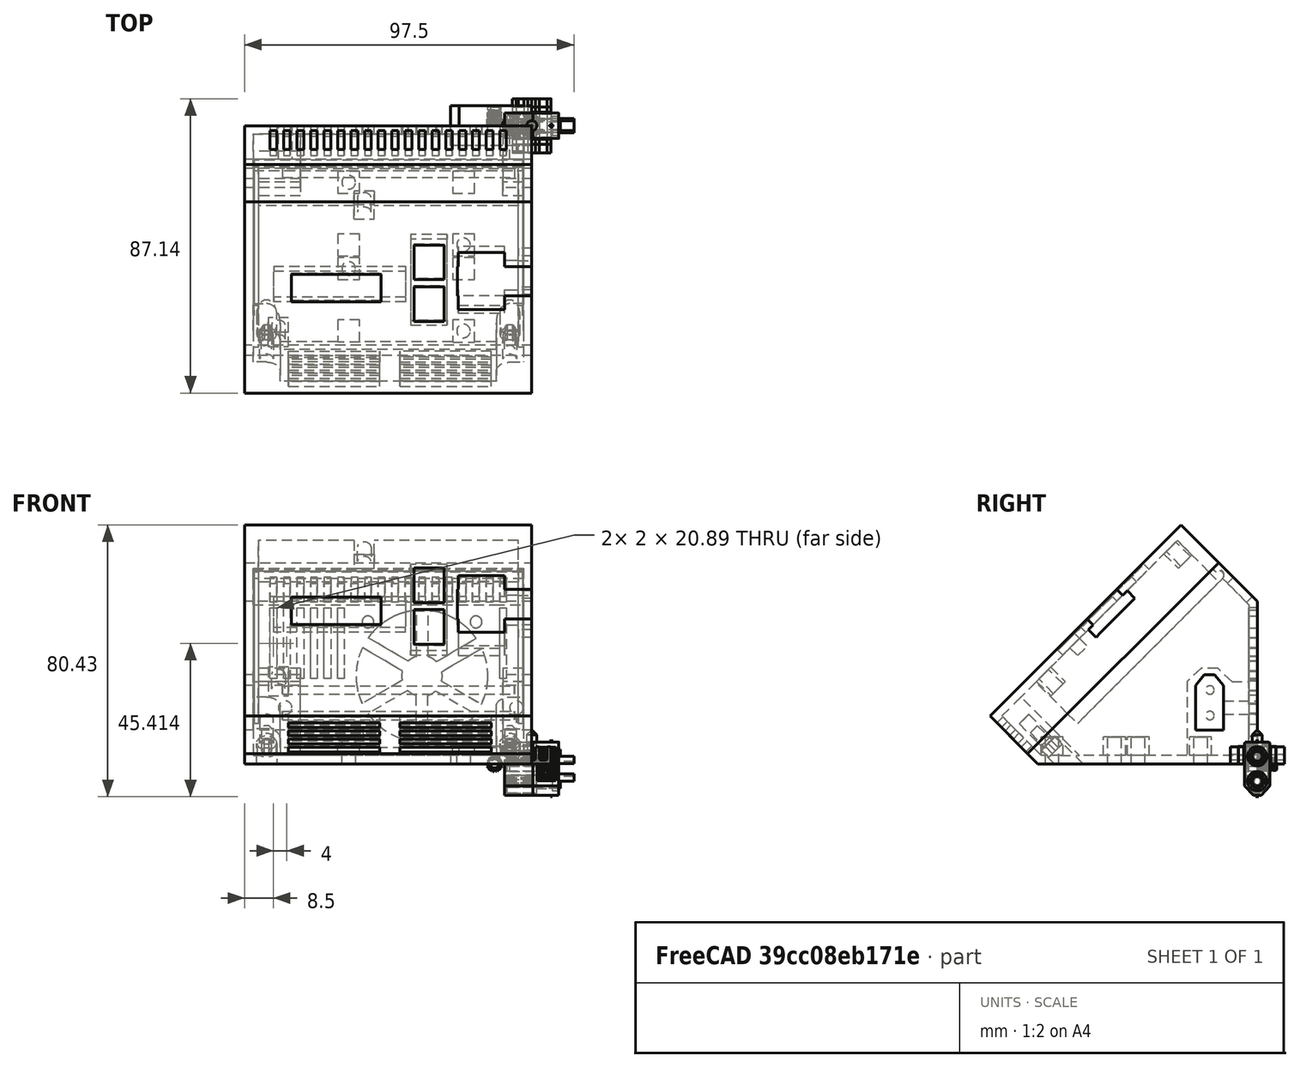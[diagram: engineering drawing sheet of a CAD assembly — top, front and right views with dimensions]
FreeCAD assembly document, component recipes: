
FREECAD ASSEMBLY — COMPONENT RECIPES ("moduleUSB3A_023_SurBase35mm_013")

This assembly document has 20 components, labeled P0..P19 below (a component is one placed body or linked part). 13 of them carry a construction recipe — the FreeCAD feature program that regenerates the part from scratch, quoted from this document or its linked companion documents; the rest are supplied as boundary geometry only. No exploded tour is included for this assembly.
COMPONENT P0 — recipe-attached ("base", modeled in this document).
Construction recipe (the document's own serialized feature program — sketch geometry with constraints, then the solid features built on it; lengths are millimeters unless a unit is written):

FEATURE [PartDesign::FeatureBase] Clone
  BaseFeature = -> Slice_child0
FEATURE [PartDesign::Thickness] Thickness
  Base = -> Clone [Face7]
  BaseFeature = -> Clone
  Intersection = false
  Join = 0
  Mode = 0
  Reversed = true
  SupportTransform = false
  Value = 2.5
  expr: Value = <<sp>>.epaisseurParois
FEATURE [PartDesign::Plane] DatumPlane001  label="planXt"
  AttachmentOffset = pos=(0,0,-2.5) rot=(0,0,1;0rad)
  Length = 110.737
  MapMode = 5
  Placement = pos=(-2.5,6e-16,-6e-16) rot=(0.57735,0.57735,0.57735;2.0944rad)
  ResizeMode = 0
  Support = -> [YZ_Plane002]
  Width = 102.305
  expr: .AttachmentOffset.Base.z = -<<sp>>.epaisseurParois
FEATURE [Sketcher::SketchObject] Sketch002  label="sk_renfortXt"
  FullyConstrained = true
  MapMode = 5
  Placement = pos=(-2.5,6e-16,-6e-16) rot=(0.57735,0.57735,0.57735;2.0944rad)
  Support = -> [DatumPlane001]
  expr: .Constraints.dist = <<sp>>.xt60distanceAngleBord
  expr: .Constraints.epRf = <<sp>>.xt60epRenfort
  expr: Constraints[13] = <<sp>>.xt60largeurFetiere
  expr: Constraints[14] = <<sp>>.xt60hauteur
  expr: Constraints[15] = <<sp>>.xt60hauteurToit
  expr: Constraints[16] = <<sp>>.xt60base
  expr: Constraints[18] = .Constraints.dist
  expr: Constraints[31] = <<sp>>.epaisseurParois
  expr: Constraints[32] = .Constraints.epRf
  expr: Constraints[34] = .Constraints.epRf
  expr: Constraints[45] = <<sp>>.epaisseurParois
  sketch-geometry (17):
    g0: LineSegment StartX=-18.3 StartY=10 StartZ=0 EndX=-18.3 EndY=23.25 EndZ=0
    g1: LineSegment StartX=-18.3 StartY=23.25 StartZ=0 EndX=-15.65 EndY=25.75 EndZ=0
    g2: LineSegment StartX=-15.65 StartY=25.75 StartZ=0 EndX=-12.65 EndY=25.75 EndZ=0
    g3: LineSegment StartX=-12.65 StartY=25.75 StartZ=0 EndX=-10 EndY=23.25 EndZ=0
    g4: LineSegment StartX=-10 StartY=23.25 StartZ=0 EndX=-10 EndY=10 EndZ=0
    g5: LineSegment StartX=-10 StartY=10 StartZ=0 EndX=-18.3 EndY=10 EndZ=0
    g6: LineSegment StartX=-14.15 StartY=10 StartZ=0 EndX=-14.15 EndY=25.75 EndZ=0
    g7: LineSegment StartX=-16.6431 StartY=28.25 StartZ=0 EndX=-20.8 EndY=24.3284 EndZ=0
    g8: LineSegment StartX=-20.8 StartY=24.3284 StartZ=0 EndX=-20.8 EndY=2.5 EndZ=0
    g9: LineSegment StartX=-20.8 StartY=2.5 StartZ=0 EndX=-7.5 EndY=2.5 EndZ=0
    g10: LineSegment StartX=-7.5 StartY=2.5 StartZ=0 EndX=-7.5 EndY=24.3284 EndZ=0
    g11: LineSegment StartX=-7.5 StartY=24.3284 StartZ=0 EndX=-11.6569 EndY=28.25 EndZ=0
    g12: LineSegment StartX=-11.6569 StartY=28.25 StartZ=0 EndX=-16.6431 EndY=28.25 EndZ=0
    g13: LineSegment StartX=-7.5 StartY=24.3284 StartZ=0 EndX=-2.5 EndY=24.3284 EndZ=0
    g14: LineSegment StartX=-2.5 StartY=24.3284 StartZ=0 EndX=-2.5 EndY=2.5 EndZ=0
    g15: LineSegment StartX=-2.5 StartY=2.5 StartZ=0 EndX=-7.5 EndY=2.5 EndZ=0
    g16: LineSegment StartX=-7.5 StartY=2.5 StartZ=0 EndX=-7.5 EndY=24.3284 EndZ=0
  constraints (46):
    c: Vertical(g0)
    c: Coincident(g0,g1)
    c: Coincident(g1,g2)
    c: Horizontal(g2)
    c: Coincident(g2,g3)
    c: Coincident(g3,g4)
    c: Vertical(g4)
    c: Coincident(g4,g5)
    c: Coincident(g5,g0)
    c: Horizontal(g5)
    c: Symmetric(g1,g2,g6)
    c: Equal(g0,g4)
    c: Symmetric(g0,g4,g6)
    c: DistanceX(g2,g2) = 3
    c: DistanceY(g4,g4) = 13.25
    c: DistanceY(g3,g2) = 2.5
    c: DistanceX(g5,g5) = 8.3
    c: DistanceX(g4,g-1) = 10  'dist'
    c: DistanceY(g-1,g4) = 10
    c: Coincident(g7,g8)
    c: Vertical(g8)
    c: Coincident(g8,g9)
    c: Horizontal(g9)
    c: Coincident(g9,g10)
    c: Coincident(g10,g11)
    c: Coincident(g11,g12)
    c: Coincident(g12,g7)
    c: Symmetric(g7,g10,g6)
    c: Symmetric(g7,g11,g6)
    c: Symmetric(g8,g9,g6)
    c: DistanceX(g8,g0) = 2.5  'epRf'
    c: DistanceY(g-1,g9) = 2.5
    c: Distance(g7,g1) = 2.5
    c: Parallel(g1,g7)
    c: DistanceY(g2,g11) = 2.5
    c: Coincident(g13,g14)
    c: Coincident(g14,g15)
    c: Coincident(g15,g16)
    c: Coincident(g16,g13)
    c: Horizontal(g13)
    c: Horizontal(g15)
    c: Vertical(g14)
    c: Vertical(g16)
    c: Coincident(g13,g11)
    c: Horizontal(g14,g9)
    c: DistanceX(g14,g-1) = 2.5
FEATURE [PartDesign::Pad] Pad001  label="renfortXt"
  AllowMultiFace = false
  BaseFeature = -> Thickness
  Direction = (1,-1e-16,1e-16)
  Length = 80
  Length2 = 100
  Profile = -> Sketch002
  Reversed = true
  Type = 0
  expr: Length = <<sp>>.largeurModuleBase - 2 * <<sp>>.epaisseurParois
FEATURE [Sketcher::SketchObject] Sketch003  label="sk_trouXt"
  FullyConstrained = true
  MapMode = 5
  Placement = pos=(0,0,0) rot=(0.57735,0.57735,0.57735;2.0944rad)
  Support = -> [YZ_Plane002]
  expr: .Constraints.dist = <<sp>>.xt60distanceAngleBord
  expr: Constraints[13] = <<sp>>.xt60base
  expr: Constraints[14] = <<sp>>.xt60hauteur
  expr: Constraints[15] = <<sp>>.xt60hauteurToit + <<sp>>.xtJeu
  expr: Constraints[16] = <<sp>>.xt60largeurFetiere
  expr: Constraints[18] = .Constraints.dist
  sketch-geometry (7):
    g0: LineSegment StartX=-18.3 StartY=10 StartZ=0 EndX=-18.3 EndY=23.25 EndZ=0
    g1: LineSegment StartX=-18.3 StartY=23.25 StartZ=0 EndX=-15.65 EndY=26.35 EndZ=0
    g2: LineSegment StartX=-15.65 StartY=26.35 StartZ=0 EndX=-12.65 EndY=26.35 EndZ=0
    g3: LineSegment StartX=-12.65 StartY=26.35 StartZ=0 EndX=-10 EndY=23.25 EndZ=0
    g4: LineSegment StartX=-10 StartY=23.25 StartZ=0 EndX=-10 EndY=10 EndZ=0
    g5: LineSegment StartX=-10 StartY=10 StartZ=0 EndX=-18.3 EndY=10 EndZ=0
    g6: LineSegment StartX=-14.15 StartY=10 StartZ=0 EndX=-14.15 EndY=26.35 EndZ=0
  constraints (19):
    c: Vertical(g0)
    c: Coincident(g0,g1)
    c: Coincident(g1,g2)
    c: Horizontal(g2)
    c: Coincident(g2,g3)
    c: Coincident(g3,g4)
    c: Coincident(g4,g5)
    c: Coincident(g5,g0)
    c: Horizontal(g5)
    c: Symmetric(g1,g2,g6)
    c: Symmetric(g0,g3,g6)
    c: Vertical(g6)
    c: Symmetric(g0,g4,g6)
    c: DistanceX(g5,g5) = 8.3
    c: DistanceY(g4,g4) = 13.25
    c: DistanceY(g3,g2) = 3.1
    c: DistanceX(g2,g2) = 3
    c: DistanceX(g4,g-1) = 10  'dist'
    c: DistanceY(g-1,g4) = 10
FEATURE [PartDesign::Pocket] Pocket
  AllowMultiFace = false
  BaseFeature = -> Pad001
  Direction = (-1,2e-16,-3e-16)
  Length = 85
  Length2 = 100
  Profile = -> Sketch003
  Type = 0
  expr: Length = <<sp>>.largeurModuleBase
FEATURE [PartDesign::Plane] DatumPlane002  label="planDecoupeRenfortXt"
  AttachmentOffset = pos=(0,0,2.5) rot=(0,0,1;0rad)
  Length = 129.29
  MapMode = 5
  Placement = pos=(0,-2.5,-6e-16) rot=(1,0,0;1.5708rad)
  ResizeMode = 0
  Support = -> [XZ_Plane002]
  Width = 103.858
  expr: .AttachmentOffset.Base.z = <<sp>>.epaisseurParois
FEATURE [Sketcher::SketchObject] Sketch004  label="sk_decoupRenfXt"
  FullyConstrained = true
  MapMode = 5
  Placement = pos=(0,-2.5,-6e-16) rot=(1,0,0;1.5708rad)
  Support = -> [DatumPlane002]
  expr: Constraints[10] = <<sp>>.xt60LongueurRenfortPetit + <<sp>>.epaisseurParois
  expr: Constraints[11] = <<sp>>.largeurModuleBase - (<<sp>>.xt60longueurRenfortGrand + <<sp>>.epaisseurParois)
  expr: Constraints[8] = <<sp>>.epaisseurParois
  expr: Constraints[9] = <<sp>>.xt60distanceAngleBord + <<sp>>.xt60hauteur + <<sp>>.xt60hauteurToit + <<sp>>.xt60epRenfort
  sketch-geometry (4):
    g0: LineSegment StartX=-68.5 StartY=28.25 StartZ=0 EndX=-8.5 EndY=28.25 EndZ=0
    g1: LineSegment StartX=-8.5 StartY=28.25 StartZ=0 EndX=-8.5 EndY=2.5 EndZ=0
    g2: LineSegment StartX=-8.5 StartY=2.5 StartZ=0 EndX=-68.5 EndY=2.5 EndZ=0
    g3: LineSegment StartX=-68.5 StartY=2.5 StartZ=0 EndX=-68.5 EndY=28.25 EndZ=0
  constraints (12):
    c: Coincident(g0,g1)
    c: Coincident(g1,g2)
    c: Coincident(g2,g3)
    c: Coincident(g3,g0)
    c: Horizontal(g0)
    c: Horizontal(g2)
    c: Vertical(g1)
    c: Vertical(g3)
    c: DistanceY(g-1,g1) = 2.5
    c: DistanceY(g-1,g0) = 28.25
    c: DistanceX(g1,g-1) = 8.5
    c: DistanceX(g2,g-1) = 68.5
FEATURE [PartDesign::Pocket] Pocket001  label="decoupeRenfXt"
  AllowMultiFace = false
  BaseFeature = -> Pocket
  Direction = (0,1,2e-16)
  Length = 23.3
  Length2 = 100
  Profile = -> Sketch004
  Reversed = true
  Type = 0
  expr: Length = <<sp>>.xt60distanceAngleBord + <<sp>>.xt60base + 2 * <<sp>>.xt60epRenfort
FEATURE [Sketcher::SketchObject] Sketch005  label="xt60PercagePostMale"
  FullyConstrained = true
  MapMode = 5
  Placement = pos=(0,0,0) rot=(1,0,0;1.5708rad)
  Support = -> [XZ_Plane002]
  expr: Constraints[0] = <<sp>>.insertDiamPercage
  expr: Constraints[1] = <<sp>>.insertDistanceTrouBordMale
  expr: Constraints[2] = <<sp>>.insertHauteur
  sketch-geometry (1):
    g0: Circle CenterX=-4.5 CenterY=16.625 CenterZ=0 NormalX=0 NormalY=0 NormalZ=1 AngleXU=0 Radius=2
  constraints (3):
    c: Diameter(g0) = 4
    c: DistanceX(g0,g-1) = 4.5
    c: DistanceY(g-1,g0) = 16.625
FEATURE [PartDesign::Pocket] Pocket002  label="insertXtMale"
  AllowMultiFace = false
  BaseFeature = -> Pocket001
  Direction = (0,1,2e-16)
  Length = 10
  Length2 = 100
  Profile = -> Sketch005
  Reversed = true
  Type = 0
  expr: Length = <<sp>>.insertProfondeurPercage
FEATURE [Sketcher::SketchObject] Sketch006  label="xt60PercagePostFem"
  FullyConstrained = true
  MapMode = 5
  Placement = pos=(0,0,0) rot=(1,0,0;1.5708rad)
  Support = -> [XZ_Plane002]
  expr: Constraints[0] = <<sp>>.insertDiamPercage
  expr: Constraints[1] = <<sp>>.insertDistanceTrouBordFem
  expr: Constraints[2] = <<sp>>.insertHauteur
  sketch-geometry (1):
    g0: Circle CenterX=-73 CenterY=16.625 CenterZ=0 NormalX=0 NormalY=0 NormalZ=1 AngleXU=0 Radius=2
  constraints (3):
    c: Diameter(g0) = 4
    c: DistanceX(g0,g-1) = 73
    c: DistanceY(g-1,g0) = 16.625
FEATURE [PartDesign::Pocket] Pocket003  label="insertXt60Fem"
  AllowMultiFace = false
  BaseFeature = -> Pocket002
  Direction = (0,1,2e-16)
  Length = 10
  Length2 = 100
  Profile = -> Sketch006
  Reversed = true
  Type = 0
  expr: Length = <<sp>>.insertProfondeurPercage
FEATURE [PartDesign::Plane] DatumPlane003
  AttachmentOffset = pos=(0,0,2.5) rot=(0,0,1;0rad)
  Length = 130.229
  MapMode = 2
  Placement = pos=(0,0,2.5) rot=(0,0,1;0rad)
  ResizeMode = 0
  Support = -> [XY_Plane002]
  Width = 113.229
  expr: .AttachmentOffset.Base.z = <<sp>>.epaisseurParois
FEATURE [PartDesign::Plane] DatumPlane004  label="planTrancheur"
  AttachmentOffset = pos=(0,0,71) rot=(-1,0,0;0.785398rad)
  Length = 133.505
  MapMode = 5
  Placement = pos=(0,-71,-1.58e-14) rot=(1,0,0;0.785398rad)
  ResizeMode = 0
  Support = -> [XZ_Plane002]
  Width = 149.064
  expr: .AttachmentOffset.Base.z = <<sp>>.planTrancheur
FEATURE [Sketcher::SketchObject] Sketch008
  FullyConstrained = true
  MapMode = 5
  Placement = pos=(0,-71,-2.13e-14) rot=(1,0,0;0.785398rad)
  Support = -> [DatumPlane004]
  expr: .Constraints.dist = <<sp>>.epaisseurParois
  expr: Constraints[13] = <<sp>>.epaisseurParois
  expr: Constraints[16] = <<sp>>.insertDiamPercage / 2 + <<sp>>.insertFAVMargeDist
  expr: Constraints[1] = <<sp>>.insertFavDistAuZeroDuPLan
  expr: Constraints[21] = <<sp>>.insertFAVDistBord
  expr: Constraints[22] = <<sp>>.largeurModuleBase - <<sp>>.epaisseurParois
  sketch-geometry (7):
    g0: LineSegment StartX=-2.5 StartY=4.24264 StartZ=0 EndX=-82.5 EndY=4.24264 EndZ=0
    g1: LineSegment StartX=-6.5 StartY=14.7426 StartZ=0 EndX=-2.5 EndY=14.7426 EndZ=0
    g2: LineSegment StartX=-2.5 StartY=14.7426 StartZ=0 EndX=-2.5 EndY=6.74264 EndZ=0
    g3: LineSegment StartX=-2.5 StartY=6.74264 StartZ=0 EndX=-10.5 EndY=6.74264 EndZ=0
    g4: LineSegment StartX=-10.5 StartY=6.74264 StartZ=0 EndX=-10.5 EndY=10.7426 EndZ=0
    g5: ArcOfCircle CenterX=-6.5 CenterY=10.7426 CenterZ=0 NormalX=0 NormalY=0 NormalZ=1 AngleXU=0 Radius=4 StartAngle=1.5708 EndAngle=3.14159
    g6: LineSegment StartX=-6.5 StartY=10.7426 StartZ=0 EndX=-6.5 EndY=6.74264 EndZ=0
  constraints (23):
    c: Horizontal(g0)
    c: DistanceY(g-1,g0) = 4.24264
    c: DistanceX(g0,g-1) = 2.5  'dist'
    c: Horizontal(g1)
    c: Coincident(g1,g2)
    c: Vertical(g2)
    c: Coincident(g2,g3)
    c: Horizontal(g3)
    c: Coincident(g3,g4)
    c: Vertical(g4)
    c: Vertical(g2,g0)
    c: Equal(g3,g2)
    c: Equal(g4,g1)
    c: DistanceY(g0,g2) = 2.5
    c: Coincident(g5,g4)
    c: Coincident(g5,g1)
    c: DistanceX(g5,g2) = 4
    c: Coincident(g6,g5)
    c: PointOnObject(g6,g3)
    c: Vertical(g6)
    c: Vertical(g5,g1)
    c: DistanceX(g3,g3) = 8
    c: DistanceX(g0,g-1) = 82.5
FEATURE [PartDesign::Pad] Pad003  label="padTrouFAVDroite"
  AllowMultiFace = false
  BaseFeature = -> Pocket003
  Direction = (0,-0.707107,0.707107)
  Length = 10
  Length2 = 100
  Profile = -> Sketch008
  Reversed = true
  Type = 3
  UpToFace = -> DatumPlane003
FEATURE [Sketcher::SketchObject] Sketch009
  FullyConstrained = true
  MapMode = 5
  Placement = pos=(0,-71,-2.13e-14) rot=(1,0,0;0.785398rad)
  Support = -> [DatumPlane004]
  expr: .Constraints.larg = <<sp>>.insertFAVDistBord
  expr: Constraints[11] = .Constraints.larg / 2
  expr: Constraints[12] = <<sp>>.largeurModuleBase
  expr: Constraints[13] = <<sp>>.insertFavDistAuZeroDuPLan
  expr: Constraints[14] = <<sp>>.epaisseurParois
  expr: Constraints[15] = <<sp>>.epaisseurParois
  expr: Constraints[8] = .Constraints.larg
  sketch-geometry (6):
    g0: LineSegment StartX=-82.5 StartY=6.74264 StartZ=0 EndX=-74.5 EndY=6.74264 EndZ=0
    g1: LineSegment StartX=-74.5 StartY=6.74264 StartZ=0 EndX=-74.5 EndY=10.7426 EndZ=0
    g2: LineSegment StartX=-78.5 StartY=14.7426 StartZ=0 EndX=-82.5 EndY=14.7426 EndZ=0
    g3: LineSegment StartX=-82.5 StartY=14.7426 StartZ=0 EndX=-82.5 EndY=6.74264 EndZ=0
    g4: ArcOfCircle CenterX=-78.5 CenterY=10.7426 CenterZ=0 NormalX=0 NormalY=0 NormalZ=1 AngleXU=0 Radius=4 StartAngle=1e-16 EndAngle=1.5708
    g5: GeomPoint X=-85 Y=4.24264 Z=0
  constraints (16):
    c: Coincident(g0,g1)
    c: Coincident(g2,g3)
    c: Coincident(g3,g0)
    c: Horizontal(g0)
    c: Horizontal(g2)
    c: Vertical(g1)
    c: Vertical(g3)
    c: DistanceX(g0,g0) = 8  'larg'
    c: DistanceY(g3,g3) = 8
    c: Tangent(g2,g4) = -1.5708
    c: Tangent(g1,g4) = -1.5708
    c: DistanceX(g0,g4) = 4
    c: DistanceX(g5,g-1) = 85
    c: DistanceY(g-1,g5) = 4.24264
    c: DistanceX(g5,g0) = 2.5
    c: DistanceY(g5,g0) = 2.5
FEATURE [PartDesign::Pad] Pad004  label="padTrouFavGauche"
  AllowMultiFace = false
  BaseFeature = -> Pad003
  Direction = (0,-0.707107,0.707107)
  Length = 10
  Length2 = 100
  Profile = -> Sketch009
  Type = 3
  UpToFace = -> DatumPlane003 [Plane]
FEATURE [Sketcher::SketchObject] Sketch010
  FullyConstrained = true
  MapMode = 5
  Placement = pos=(0,-71,-2.13e-14) rot=(1,0,0;0.785398rad)
  Support = -> [DatumPlane004]
  expr: Constraints[0] = <<sp>>.insertFAVDistBord / 2 + <<sp>>.epaisseurParois
  expr: Constraints[1] = <<sp>>.insertFavDistAuZeroDuPLan + <<sp>>.epaisseurParois + <<sp>>.insertFAVDistBord / 2
  expr: Constraints[2] = <<sp>>.insertDiamPercage
  sketch-geometry (1):
    g0: Circle CenterX=-6.5 CenterY=10.7426 CenterZ=0 NormalX=0 NormalY=0 NormalZ=1 AngleXU=0 Radius=2
  constraints (3):
    c: DistanceX(g0,g-1) = 6.5
    c: DistanceY(g-1,g0) = 10.7426
    c: Diameter(g0) = 4
FEATURE [PartDesign::Pocket] Pocket004  label="trouDroit"
  AllowMultiFace = false
  BaseFeature = -> Pad004
  Direction = (0,0.707107,-0.707107)
  Length = 5
  Length2 = 100
  Profile = -> Sketch010
  Type = 1
FEATURE [Sketcher::SketchObject] Sketch011
  FullyConstrained = true
  MapMode = 5
  Placement = pos=(0,-71,-2.13e-14) rot=(1,0,0;0.785398rad)
  Support = -> [DatumPlane004]
  expr: Constraints[0] = <<sp>>.insertDiamPercage
  expr: Constraints[1] = <<sp>>.largeurModuleBase - <<sp>>.epaisseurParois - <<sp>>.insertFAVDistBord / 2
  expr: Constraints[2] = <<sp>>.insertFavDistAuZeroDuPLan + <<sp>>.epaisseurParois + <<sp>>.insertFAVDistBord / 2
  sketch-geometry (1):
    g0: Circle CenterX=-78.5 CenterY=10.7426 CenterZ=0 NormalX=0 NormalY=0 NormalZ=1 AngleXU=0 Radius=2
  constraints (3):
    c: Diameter(g0) = 4
    c: DistanceX(g0,g-1) = 78.5
    c: DistanceY(g-1,g0) = 10.7426
FEATURE [PartDesign::Pocket] Pocket005  label="trouGauche"
  AllowMultiFace = false
  BaseFeature = -> Pocket004
  Direction = (0,0.707107,-0.707107)
  Length = 5
  Length2 = 100
  Profile = -> Sketch011
  Type = 1
FEATURE [PartDesign::Plane] DatumPlane005  label="planTeteVisFav"
  AttachmentOffset = pos=(0,0,68) rot=(-1,0,0;0.785398rad)
  Length = 133.505
  MapMode = 5
  Placement = pos=(0,-68,-1.51e-14) rot=(1,0,0;0.785398rad)
  ResizeMode = 0
  Support = -> [XZ_Plane002]
  Width = 149.064
  expr: .AttachmentOffset.Base.z = <<sp>>.planTrancheur - 3
FEATURE [Sketcher::SketchObject] Sketch012
  ExternalGeometry = -> [Pocket005]
  FullyConstrained = true
  MapMode = 5
  Placement = pos=(0,-68,-1.42e-14) rot=(1,0,0;0.785398rad)
  Support = -> [DatumPlane005]
  expr: Constraints[1] = <<sp>>.visM3DiamEncastrement
  sketch-geometry (2):
    g0: Circle CenterX=-6.5 CenterY=8.62132 CenterZ=0 NormalX=0 NormalY=0 NormalZ=1 AngleXU=0 Radius=3
    g1: Circle CenterX=-78.5 CenterY=8.62132 CenterZ=0 NormalX=0 NormalY=0 NormalZ=1 AngleXU=0 Radius=3
  constraints (4):
    c: Equal(g0,g1)
    c: Diameter(g1) = 6
    c: Coincident(g1,g-4)
    c: Coincident(g-3,g0)
FEATURE [PartDesign::Pocket] Pocket006  label="evidementTeteVisFav"
  AllowMultiFace = false
  BaseFeature = -> Pocket005
  Direction = (0,0.707107,-0.707107)
  Length = 20
  Length2 = 100
  Profile = -> Sketch012
  Type = 1
FEATURE [Sketcher::SketchObject] Sketch014
  FullyConstrained = true
  MapMode = 5
  Placement = pos=(0,0,0) rot=(1,0,0;1.5708rad)
  Support = -> [XZ_Plane002]
  expr: Constraints[12] = <<sp>>.xt60distanceAngleBord + <<sp>>.xt60hauteur + <<sp>>.ventilDistBordFente
  expr: Constraints[13] = <<sp>>.ventilLargeurFentes
  expr: Constraints[14] = <<sp>>.ventilEcartfente / 2
  expr: Constraints[15] = <<sp>>.hauteurDuDos - <<sp>>.ventilDistBordFente
  expr: Constraints[2] = <<sp>>.hauteurDuDos
  expr: Constraints[3] = <<sp>>.largeurModuleBase / 2
  sketch-geometry (5):
    g0: LineSegment StartX=-42.5 StartY=0 StartZ=0 EndX=-42.5 EndY=48.1371 EndZ=0
    g1: LineSegment StartX=-45.5 StartY=46.1371 StartZ=0 EndX=-43.5 EndY=46.1371 EndZ=0
    g2: LineSegment StartX=-43.5 StartY=46.1371 StartZ=0 EndX=-43.5 EndY=25.25 EndZ=0
    g3: LineSegment StartX=-43.5 StartY=25.25 StartZ=0 EndX=-45.5 EndY=25.25 EndZ=0
    g4: LineSegment StartX=-45.5 StartY=25.25 StartZ=0 EndX=-45.5 EndY=46.1371 EndZ=0
  constraints (16):
    c: PointOnObject(g0,g-1)
    c: Vertical(g0)
    c: DistanceY(g0,g0) = 48.1371
    c: DistanceX(g0,g-1) = 42.5
    c: Coincident(g1,g2)
    c: Coincident(g2,g3)
    c: Coincident(g3,g4)
    c: Coincident(g4,g1)
    c: Horizontal(g1)
    c: Horizontal(g3)
    c: Vertical(g2)
    c: Vertical(g4)
    c: DistanceY(g-1,g2) = 25.25
    c: DistanceX(g1,g1) = 2
    c: DistanceX(g2,g0) = 1
    c: DistanceY(g-1,g1) = 46.1371
FEATURE [PartDesign::Pocket] Pocket008  label="ventilFente1"
  AllowMultiFace = false
  BaseFeature = -> Pocket006
  Direction = (0,1,2e-16)
  Length = 2.5
  Length2 = 100
  Profile = -> Sketch014
  Reversed = true
  Type = 0
  expr: Length = <<sp>>.epaisseurParois
FEATURE [PartDesign::LinearPattern] LinearPattern  label="ventilDosRepeat1"
  BaseFeature = -> Pocket008
  Direction = -> Sketch014 [H_Axis]
  Length = 32
  Occurrences = 9
  Originals = -> [Pocket008]
  Reversed = true
  expr: Length = <<sp>>.ventilLargeurRepet
  expr: Occurrences = <<sp>>.ventilNbrFents
FEATURE [PartDesign::LinearPattern] LinearPattern001  label="ventilDosRepeat2"
  BaseFeature = -> LinearPattern
  Direction = -> Sketch014 [H_Axis]
  Length = 36
  Occurrences = 10
  Originals = -> [Pocket008]
  expr: Length = <<sp>>.ventilLargeurRepet + <<sp>>.ventilEcartfente + <<sp>>.ventilLargeurFentes
  expr: Occurrences = <<sp>>.ventilNbrFents + 1
FEATURE [PartDesign::Plane] DatumPlane006  label="planVentilSup"
  AttachmentOffset = pos=(0,0,-48.1371) rot=(1,0,0;0.785398rad)
  Length = 133.505
  MapMode = 5
  Placement = pos=(0,48.1371,1.07e-14) rot=(1,0,0;2.35619rad)
  ResizeMode = 0
  Support = -> [XZ_Plane002]
  Width = 149.064
  expr: .AttachmentOffset.Base.z = -<<sp>>.hauteurDuDos
FEATURE [Sketcher::SketchObject] Sketch015
  FullyConstrained = true
  MapMode = 5
  Placement = pos=(0,48.1371,1.07e-14) rot=(1,0,0;2.35619rad)
  Support = -> [DatumPlane006]
  expr: Constraints[10] = <<sp>>.ventilLargeurFentes
  expr: Constraints[11] = (<<sp>>.largeurModuleBase + <<sp>>.ventilEcartfente) / 2
  expr: Constraints[8] = <<sp>>.distanceAuZeroPlanBorArriere + <<sp>>.ventilDistBordFente
  expr: Constraints[9] = <<sp>>.longPetitRetSupSansFav - 2 * <<sp>>.ventilDistBordFente - <<sp>>.favBordureProf
  sketch-geometry (4):
    g0: LineSegment StartX=-43.5 StartY=78.0926 StartZ=0 EndX=-45.5 EndY=78.0926 EndZ=0
    g1: LineSegment StartX=-45.5 StartY=78.0926 StartZ=0 EndX=-45.5 EndY=70.0761 EndZ=0
    g2: LineSegment StartX=-45.5 StartY=70.0761 StartZ=0 EndX=-43.5 EndY=70.0761 EndZ=0
    g3: LineSegment StartX=-43.5 StartY=70.0761 StartZ=0 EndX=-43.5 EndY=78.0926 EndZ=0
  constraints (12):
    c: Coincident(g0,g1)
    c: Coincident(g1,g2)
    c: Coincident(g2,g3)
    c: Coincident(g3,g0)
    c: Horizontal(g0)
    c: Horizontal(g2)
    c: Vertical(g1)
    c: Vertical(g3)
    c: DistanceY(g-1,g2) = 70.0761
    c: DistanceY(g2,g0) = 8.01652
    c: DistanceX(g0,g0) = 2
    c: DistanceX(g2,g-1) = 43.5
FEATURE [PartDesign::Pocket] Pocket009  label="ventilSupFente"
  AllowMultiFace = false
  BaseFeature = -> LinearPattern001
  Direction = (0,0.707107,0.707107)
  Length = 5
  Length2 = 100
  Profile = -> Sketch015
  Reversed = true
  Type = 0
FEATURE [PartDesign::LinearPattern] LinearPattern002  label="ventilSupRepeat1"
  BaseFeature = -> Pocket009
  Direction = -> Sketch015 [H_Axis]
  Length = 32
  Occurrences = 9
  Originals = -> [Pocket009]
  Reversed = true
  expr: Length = <<sp>>.ventilLargeurRepet
  expr: Occurrences = <<sp>>.ventilNbrFents
FEATURE [PartDesign::LinearPattern] LinearPattern003  label="ventilSupRepeat2"
  BaseFeature = -> LinearPattern002
  Direction = -> Sketch015 [H_Axis]
  Length = 36
  Occurrences = 10
  Originals = -> [Pocket009]
  expr: Length = <<sp>>.ventilLargeurRepet + <<sp>>.ventilEcartfente + <<sp>>.ventilLargeurFentes
  expr: Occurrences = <<sp>>.ventilNbrFents + 1
FEATURE [PartDesign::Body] Body001  label="base"
  BaseFeature = -> Slice_child0
  Group = -> [Clone,Thickness,DatumPlane001,Sketch002,Pad001,Sketch003,Pocket,DatumPlane002,Sketch004,Pocket001,Sketch005,Pocket002,Sketch006,Pocket003,DatumPlane003,DatumPlane004,Sketch008,Pad003,Sketch009,Pad004,Sketch010,Pocket004,Sketch011,Pocket005,DatumPlane005,Sketch012,Pocket006,Sketch014,Pocket008,LinearPattern,LinearPattern001,DatumPlane006,Sketch015,Pocket009,LinearPattern002,LinearPattern003,+14 more]
  Origin = -> Origin002
  Tip = -> PolarPattern
COMPONENT P1 — recipe-attached ("faceAvant", modeled in this document).
Construction recipe (the document's own serialized feature program — sketch geometry with constraints, then the solid features built on it; lengths are millimeters unless a unit is written):

FEATURE [PartDesign::FeatureBase] Clone001
  BaseFeature = -> Slice_child1
FEATURE [PartDesign::Thickness] Thickness001
  Base = -> Clone001 [Face5]
  BaseFeature = -> Clone001
  Intersection = false
  Join = 0
  Mode = 0
  Reversed = true
  SupportTransform = false
  Value = 2.5
  expr: Value = <<sp>>.epaisseurParois
FEATURE [PartDesign::Plane] DatumPlane007  label="planTrancheurBis"
  AttachmentOffset = pos=(0,0,71) rot=(-1,0,0;0.785398rad)
  Length = 134.936
  MapMode = 5
  Placement = pos=(0,-71,-1.58e-14) rot=(1,0,0;0.785398rad)
  ResizeMode = 0
  Support = -> [XZ_Plane003]
  Width = 166.253
  expr: .AttachmentOffset.Base.z = <<sp>>.planTrancheur
FEATURE [Sketcher::SketchObject] Sketch016  label="sk_insertFavDroit"
  FullyConstrained = true
  MapMode = 5
  Placement = pos=(0,-71,-2.13e-14) rot=(1,0,0;0.785398rad)
  Support = -> [DatumPlane007]
  expr: Constraints[11] = <<sp>>.insertFAVDistBord
  expr: Constraints[14] = <<sp>>.insertFAVDistBord / 2
  expr: Constraints[7] = <<sp>>.epaisseurParois
  expr: Constraints[8] = <<sp>>.insertFavDistAuZeroDuPLan + <<sp>>.epaisseurParois
  expr: Constraints[9] = <<sp>>.insertFAVDistBord
  sketch-geometry (5):
    g0: LineSegment StartX=-6.5 StartY=14.7426 StartZ=0 EndX=-2.5 EndY=14.7426 EndZ=0
    g1: LineSegment StartX=-2.5 StartY=14.7426 StartZ=0 EndX=-2.5 EndY=6.74264 EndZ=0
    g2: LineSegment StartX=-2.5 StartY=6.74264 StartZ=0 EndX=-10.5 EndY=6.74264 EndZ=0
    g3: LineSegment StartX=-10.5 StartY=6.74264 StartZ=0 EndX=-10.5 EndY=10.7426 EndZ=0
    g4: ArcOfCircle CenterX=-6.5 CenterY=10.7426 CenterZ=0 NormalX=0 NormalY=0 NormalZ=1 AngleXU=0 Radius=4 StartAngle=1.5708 EndAngle=3.14159
  constraints (15):
    c: Horizontal(g0)
    c: Coincident(g0,g1)
    c: Vertical(g1)
    c: Coincident(g1,g2)
    c: Horizontal(g2)
    c: Coincident(g2,g3)
    c: Vertical(g3)
    c: DistanceX(g1,g-1) = 2.5
    c: DistanceY(g-1,g1) = 6.74264
    c: DistanceY(g1,g1) = 8
    c: Equal(g3,g0)
    c: DistanceX(g2,g2) = 8
    c: Coincident(g4,g0)
    c: Tangent(g4,g3) = 1.5708
    c: DistanceX(g4,g1) = 4
FEATURE [PartDesign::Pad] Pad005  label="padInsertFavDroit"
  AllowMultiFace = false
  BaseFeature = -> Thickness001
  Direction = (0,-0.707107,0.707107)
  Length = 10
  Length2 = 100
  Profile = -> Sketch016
  Type = 2
FEATURE [Sketcher::SketchObject] Sketch017  label="sp_padInserFavGauch"
  FullyConstrained = true
  MapMode = 5
  Placement = pos=(0,-71,-2.13e-14) rot=(1,0,0;0.785398rad)
  Support = -> [DatumPlane007]
  expr: Constraints[10] = <<sp>>.insertFAVDistBord
  expr: Constraints[12] = <<sp>>.insertFAVDistBord / 2
  expr: Constraints[13] = <<sp>>.largeurModuleBase
  expr: Constraints[14] = <<sp>>.insertFavDistAuZeroDuPLan
  expr: Constraints[15] = <<sp>>.epaisseurParois
  expr: Constraints[16] = <<sp>>.epaisseurParois
  sketch-geometry (6):
    g0: LineSegment StartX=-78.5 StartY=14.7426 StartZ=0 EndX=-82.5 EndY=14.7426 EndZ=0
    g1: LineSegment StartX=-82.5 StartY=14.7426 StartZ=0 EndX=-82.5 EndY=6.74264 EndZ=0
    g2: LineSegment StartX=-82.5 StartY=6.74264 StartZ=0 EndX=-74.5 EndY=6.74264 EndZ=0
    g3: LineSegment StartX=-74.5 StartY=6.74264 StartZ=0 EndX=-74.5 EndY=10.7426 EndZ=0
    g4: ArcOfCircle CenterX=-78.5 CenterY=10.7426 CenterZ=0 NormalX=0 NormalY=0 NormalZ=1 AngleXU=0 Radius=4 StartAngle=0 EndAngle=1.5708
    g5: GeomPoint X=-85 Y=4.24264 Z=0
  constraints (17):
    c: Horizontal(g0)
    c: Coincident(g0,g1)
    c: Vertical(g1)
    c: Coincident(g1,g2)
    c: Horizontal(g2)
    c: Coincident(g2,g3)
    c: Vertical(g3)
    c: Equal(g3,g0)
    c: Equal(g2,g1)
    c: Coincident(g0,g4)
    c: DistanceX(g2,g2) = 8
    c: Tangent(g4,g3) = -1.5708
    c: DistanceX(g0,g0) = 4
    c: DistanceX(g5,g-1) = 85
    c: DistanceY(g-1,g5) = 4.24264
    c: DistanceY(g5,g1) = 2.5
    c: DistanceX(g5,g1) = 2.5
FEATURE [PartDesign::Pad] Pad006  label="padInsertFavGauch"
  AllowMultiFace = false
  BaseFeature = -> Pad005
  Direction = (0,-0.707107,0.707107)
  Length = 10
  Length2 = 100
  Profile = -> Sketch017
  Type = 2
FEATURE [Sketcher::SketchObject] Sketch018  label="skPercageInsertFavDroit"
  FullyConstrained = true
  MapMode = 5
  Placement = pos=(0,-71,-2.13e-14) rot=(1,0,0;0.785398rad)
  Support = -> [DatumPlane007]
  expr: Constraints[0] = <<sp>>.insertDiamPercage
  expr: Constraints[1] = <<sp>>.insertFavDistAuZeroDuPLan + <<sp>>.epaisseurParois + <<sp>>.insertFAVDistBord / 2
  expr: Constraints[2] = <<sp>>.epaisseurParois + <<sp>>.insertFAVDistBord / 2
  expr: Constraints[7] = <<sp>>.largeurModuleBase - 2 * <<sp>>.epaisseurParois - <<sp>>.insertFAVDistBord
  sketch-geometry (3):
    g0: Circle CenterX=-6.5 CenterY=10.7426 CenterZ=0 NormalX=0 NormalY=0 NormalZ=1 AngleXU=0 Radius=2
    g1: Circle CenterX=-78.5 CenterY=10.7426 CenterZ=0 NormalX=0 NormalY=0 NormalZ=1 AngleXU=0 Radius=2
    g2: LineSegment StartX=-78.5 StartY=10.7426 StartZ=0 EndX=-6.5 EndY=10.7426 EndZ=0
  constraints (8):
    c: Diameter(g0) = 4
    c: DistanceY(g-1,g0) = 10.7426
    c: DistanceX(g0,g-1) = 6.5
    c: Equal(g0,g1)
    c: Coincident(g2,g1)
    c: Coincident(g2,g0)
    c: Horizontal(g2)
    c: DistanceX(g2,g2) = 72
FEATURE [PartDesign::Pocket] Pocket010  label="trouInsertFavDroit"
  AllowMultiFace = false
  BaseFeature = -> Pad006
  Direction = (0,0.707107,-0.707107)
  Length = 8
  Length2 = 100
  Profile = -> Sketch018
  Reversed = true
  Type = 0
  expr: Length = <<sp>>.insertFavProfondeur
FEATURE [PartDesign::Plane] DatumPlane011  label="planFaceAvant"
  AttachmentOffset = pos=(0,0,93.2843) rot=(-1,0,0;0.785398rad)
  Length = 134.936
  MapMode = 5
  Placement = pos=(0,-93.2843,-2.07e-14) rot=(1,0,0;0.785398rad)
  ResizeMode = 0
  Support = -> [XZ_Plane003]
  Width = 166.253
  expr: .AttachmentOffset.Base.z = <<sp>>.planFaceAvant
FEATURE [Sketcher::SketchObject] Sketch030  label="sk_rebordFav"
  FullyConstrained = true
  MapMode = 5
  Placement = pos=(0,-71,-2.13e-14) rot=(1,0,0;0.785398rad)
  Support = -> [DatumPlane007]
  expr: Constraints[0] = <<sp>>.insertFavDistAuZeroDuPLan
  expr: Constraints[19] = <<sp>>.epaisseurParois
  expr: Constraints[20] = <<sp>>.favEpBordure
  expr: Constraints[21] = <<sp>>.favDistBordPlan
  expr: Constraints[22] = <<sp>>.largeurModuleBase - 2 * <<sp>>.epaisseurParois
  expr: Constraints[23] = <<sp>>.favEpBordure
  expr: Constraints[24] = <<sp>>.Face - <<sp>>.epaisseurParois
  expr: Constraints[25] = <<sp>>.favEpBordure
  sketch-geometry (9):
    g0: GeomPoint X=0 Y=4.24264 Z=0
    g1: LineSegment StartX=-82.5 StartY=20.9853 StartZ=0 EndX=-82.5 EndY=81.7426 EndZ=0
    g2: LineSegment StartX=-82.5 StartY=81.7426 StartZ=0 EndX=-2.5 EndY=81.7426 EndZ=0
    g3: LineSegment StartX=-2.5 StartY=81.7426 StartZ=0 EndX=-2.5 EndY=20.9853 EndZ=0
    g4: LineSegment StartX=-2.5 StartY=20.9853 StartZ=0 EndX=-4 EndY=20.9853 EndZ=0
    g5: LineSegment StartX=-4 StartY=20.9853 StartZ=0 EndX=-4 EndY=80.2426 EndZ=0
    g6: LineSegment StartX=-4 StartY=80.2426 StartZ=0 EndX=-81 EndY=80.2426 EndZ=0
    g7: LineSegment StartX=-81 StartY=80.2426 StartZ=0 EndX=-81 EndY=20.9853 EndZ=0
    g8: LineSegment StartX=-81 StartY=20.9853 StartZ=0 EndX=-82.5 EndY=20.9853 EndZ=0
  constraints (26):
    c: DistanceY(g-1,g0) = 4.24264
    c: Vertical(g0,g-1)
    c: Vertical(g1)
    c: Coincident(g1,g2)
    c: Horizontal(g2)
    c: Coincident(g2,g3)
    c: Vertical(g3)
    c: Coincident(g3,g4)
    c: Horizontal(g4)
    c: Coincident(g4,g5)
    c: Vertical(g5)
    c: Coincident(g5,g6)
    c: Horizontal(g6)
    c: Coincident(g6,g7)
    c: Vertical(g7)
    c: Coincident(g7,g8)
    c: Coincident(g8,g1)
    c: Horizontal(g8)
    c: Horizontal(g7,g4)
    c: DistanceX(g3,g0) = 2.5
    c: DistanceX(g4,g4) = 1.5
    c: DistanceY(g0,g3) = 16.7426
    c: DistanceX(g1,g3) = 80
    c: DistanceY(g5,g2) = 1.5
    c: DistanceY(g0,g2) = 77.5
    c: DistanceX(g1,g7) = 1.5
FEATURE [PartDesign::Pad] Pad014  label="favRebordSupport"
  AllowMultiFace = false
  BaseFeature = -> Pocket010
  Direction = (0,-0.707107,0.707107)
  Length = 10
  Length2 = 100
  Profile = -> Sketch030
  Type = 3
  UpToFace = -> Pocket010 [Face13]
FEATURE [PartDesign::Pad] Pad015  label="favRebord"
  AllowMultiFace = false
  BaseFeature = -> Pad014
  Direction = (0,-0.707107,0.707107)
  Length = 4.15
  Length2 = 100
  Profile = -> Sketch030
  Reversed = true
  Type = 0
  expr: Length = <<sp>>.favBordureProf
FEATURE [Sketcher::SketchObject] Sketch031  label="sk_bourlet"
  ExternalGeometry = -> [Pad015]
  FullyConstrained = true
  MapMode = 5
  Placement = pos=(-2.5,0,0) rot=(0.57735,0.57735,0.57735;2.0944rad)
  Support = -> [Pad015]
  expr: Constraints[3] = <<sp>>.bourletMaintientRayon - <<sp>>.bourletRayonJeu
  sketch-geometry (2):
    g0: ArcOfCircle CenterX=-11.184 CenterY=55.7855 CenterZ=0 NormalX=0 NormalY=0 NormalZ=1 AngleXU=0 Radius=1.3 StartAngle=5.49779 EndAngle=8.63938
    g1: LineSegment StartX=-12.1032 StartY=56.7048 StartZ=0 EndX=-10.2647 EndY=54.8663 EndZ=0
  constraints (6):
    c: Coincident(g0,g-3)
    c: PointOnObject(g0,g-3)
    c: PointOnObject(g0,g-3)
    c: Radius(g0) = 1.3
    c: Coincident(g1,g0)
    c: Coincident(g1,g0)
FEATURE [PartDesign::Pad] Pad016  label="bourlet"
  AllowMultiFace = false
  BaseFeature = -> Pad015
  Direction = (1,0,0)
  Length = 10
  Length2 = 100
  Profile = -> Sketch031
  Reversed = true
  Type = 3
  UpToFace = -> Pad015 [Face11]
FEATURE [Sketcher::SketchObject] Sketch039
  FullyConstrained = true
  MapMode = 5
  Placement = pos=(0,-71,-2.13e-14) rot=(1,0,0;0.785398rad)
  Support = -> [DatumPlane007]
  expr: Constraints[20] = <<sp>>.favBordureJeu / 2
  expr: Constraints[21] = <<sp>>.epaisseurParois
  expr: Constraints[22] = <<sp>>.largeurModuleBase - 2 * <<sp>>.epaisseurParois
  expr: Constraints[23] = <<sp>>.insertFavDistAuZeroDuPLan + <<sp>>.favDistBordPlan
  expr: Constraints[27] = <<sp>>.insertFavDistAuZeroDuPLan + <<sp>>.Face - <<sp>>.epaisseurParois + <<sp>>.bourletMaintientRayon
  sketch-geometry (10):
    g0: LineSegment StartX=-82.5 StartY=83.2426 StartZ=0 EndX=-82.25 EndY=83.2426 EndZ=0
    g1: LineSegment StartX=-82.25 StartY=83.2426 StartZ=0 EndX=-82.25 EndY=20.9853 EndZ=0
    g2: LineSegment StartX=-82.25 StartY=20.9853 StartZ=0 EndX=-82.5 EndY=20.9853 EndZ=0
    g3: LineSegment StartX=-82.5 StartY=20.9853 StartZ=0 EndX=-82.5 EndY=83.2426 EndZ=0
    g4: LineSegment StartX=-2.5 StartY=83.2426 StartZ=0 EndX=-2.75 EndY=83.2426 EndZ=0
    g5: LineSegment StartX=-2.75 StartY=83.2426 StartZ=0 EndX=-2.75 EndY=20.9853 EndZ=0
    g6: LineSegment StartX=-2.75 StartY=20.9853 StartZ=0 EndX=-2.5 EndY=20.9853 EndZ=0
    g7: LineSegment StartX=-2.5 StartY=20.9853 StartZ=0 EndX=-2.5 EndY=83.2426 EndZ=0
    g8: LineSegment StartX=-82.25 StartY=20.9853 StartZ=0 EndX=-2.5 EndY=20.9853 EndZ=0
    g9: LineSegment StartX=-2.75 StartY=83.2426 StartZ=0 EndX=-82.25 EndY=83.2426 EndZ=0
  constraints (28):
    c: Coincident(g0,g1)
    c: Coincident(g1,g2)
    c: Coincident(g2,g3)
    c: Coincident(g3,g0)
    c: Horizontal(g0)
    c: Horizontal(g2)
    c: Vertical(g1)
    c: Vertical(g3)
    c: Coincident(g4,g5)
    c: Coincident(g5,g6)
    c: Coincident(g6,g7)
    c: Coincident(g7,g4)
    c: Horizontal(g4)
    c: Horizontal(g6)
    c: Vertical(g5)
    c: Vertical(g7)
    c: Coincident(g8,g1)
    c: Coincident(g8,g6)
    c: Horizontal(g8)
    c: Equal(g2,g6)
    c: DistanceX(g2,g2) = 0.25
    c: DistanceX(g6,g-1) = 2.5
    c: DistanceX(g2,g6) = 80
    c: DistanceY(g-1,g6) = 20.9853
    c: Coincident(g9,g4)
    c: Coincident(g9,g0)
    c: Horizontal(g9)
    c: DistanceY(g-1,g4) = 83.2426
FEATURE [PartDesign::Pocket] Pocket018  label="ajoutJeuLevreFav"
  BaseFeature = -> Pad016
  Direction = (0,0.707107,-0.707107)
  Length = 4.15
  Length2 = 5
  Profile = -> Sketch039
  ReferenceAxis = -> Sketch039 [N_Axis]
  Type = 0
  expr: Length = <<sp>>.favBordureProf
FEATURE [PartDesign::Plane] DatumPlane016  label="planFaceAvantPCB"
  AttachmentOffset = pos=(0,0,84.28) rot=(-1,0,0;0.785398rad)
  Length = 134.936
  MapMode = 5
  Placement = pos=(0,-84.28,-1.87e-14) rot=(1,0,0;0.785398rad)
  ResizeMode = 0
  Support = -> [XZ_Plane003]
  Width = 166.253
FEATURE [Sketcher::SketchObject] Sketch044  label="pcbFavSk"
  FullyConstrained = false
  MapMode = 5
  Placement = pos=(0,-84.28,-1.42e-14) rot=(1,0,0;0.785398rad)
  Support = -> [DatumPlane016]
  sketch-geometry (4):
    g0: LineSegment StartX=-80.4521 StartY=87.0314 StartZ=0 EndX=-37.8912 EndY=87.0314 EndZ=0
    g1: LineSegment StartX=-37.8912 StartY=87.0314 StartZ=0 EndX=-37.8912 EndY=42.7351 EndZ=0
    g2: LineSegment StartX=-37.8912 StartY=42.7351 StartZ=0 EndX=-80.4521 EndY=42.7351 EndZ=0
    g3: LineSegment StartX=-80.4521 StartY=42.7351 StartZ=0 EndX=-80.4521 EndY=87.0314 EndZ=0
  constraints (8):
    c: Coincident(g0,g1)
    c: Coincident(g1,g2)
    c: Coincident(g2,g3)
    c: Coincident(g3,g0)
    c: Horizontal(g0)
    c: Horizontal(g2)
    c: Vertical(g1)
    c: Vertical(g3)
FEATURE [Sketcher::SketchObject] Sketch047
  FullyConstrained = true
  MapMode = 5
  Placement = pos=(0,-93.2843,-2.84e-14) rot=(1,0,0;0.785398rad)
  Support = -> [DatumPlane011]
  expr: Constraints[17] = <<sp>>.distZeroPlanFAV
  expr: Constraints[18] = <<specificSp>>.switch2PosY
  expr: Constraints[19] = <<specificSp>>.switchTrouLarg
  expr: Constraints[20] = <<specificSp>>.switchTrouLong
  expr: Constraints[24] = <<specificSp>>.switchDistY
  expr: Constraints[25] = <<specificSp>>.switch1PosX
  sketch-geometry (9):
    g0: LineSegment StartX=-34.8 StartY=82 StartZ=0 EndX=-26 EndY=82 EndZ=0
    g1: LineSegment StartX=-26 StartY=82 StartZ=0 EndX=-26 EndY=67.5 EndZ=0
    g2: LineSegment StartX=-26 StartY=67.5 StartZ=0 EndX=-34.8 EndY=67.5 EndZ=0
    g3: LineSegment StartX=-34.8 StartY=67.5 StartZ=0 EndX=-34.8 EndY=82 EndZ=0
    g4: LineSegment StartX=-34.8 StartY=64.5 StartZ=0 EndX=-26 EndY=64.5 EndZ=0
    g5: LineSegment StartX=-26 StartY=64.5 StartZ=0 EndX=-26 EndY=50 EndZ=0
    g6: LineSegment StartX=-26 StartY=50 StartZ=0 EndX=-34.8 EndY=50 EndZ=0
    g7: LineSegment StartX=-34.8 StartY=50 StartZ=0 EndX=-34.8 EndY=64.5 EndZ=0
    g8: GeomPoint X=0 Y=20 Z=0
  constraints (26):
    c: Coincident(g0,g1)
    c: Coincident(g1,g2)
    c: Coincident(g2,g3)
    c: Coincident(g3,g0)
    c: Horizontal(g0)
    c: Horizontal(g2)
    c: Vertical(g1)
    c: Vertical(g3)
    c: Coincident(g4,g5)
    c: Coincident(g5,g6)
    c: Coincident(g6,g7)
    c: Coincident(g7,g4)
    c: Horizontal(g4)
    c: Horizontal(g6)
    c: Vertical(g5)
    c: Vertical(g7)
    c: PointOnObject(g8,g-2)
    c: DistanceY(g-1,g8) = 20
    c: DistanceY(g8,g5) = 30
    c: DistanceX(g6,g5) = 8.8
    c: DistanceY(g5,g4) = 14.5
    c: Equal(g1,g5)
    c: Equal(g2,g4)
    c: Vertical(g1,g4)
    c: DistanceY(g4,g1) = 3
    c: DistanceX(g5,g-1) = 26
FEATURE [PartDesign::Pocket] Pocket022  label="switchTrous"
  BaseFeature = -> Pocket018
  Direction = (0,0.707107,-0.707107)
  Length = 2.5
  Length2 = 5
  Profile = -> Sketch047
  ReferenceAxis = -> Sketch047 [N_Axis]
  Type = 0
  expr: Length = <<sp>>.epaisseurParois
FEATURE [Sketcher::SketchObject] Sketch048
  FullyConstrained = true
  MapMode = 5
  Placement = pos=(0,-93.2843,-2.84e-14) rot=(1,0,0;0.785398rad)
  Support = -> [DatumPlane011]
  expr: Constraints[16] = <<specificSp>>.usb1PosX
  expr: Constraints[20] = <<specificSp>>.usbFenLong
  expr: Constraints[21] = <<specificSp>>.usbFenLarg
  expr: Constraints[23] = <<sp>>.distZeroPlanFAV
  expr: Constraints[24] = <<specificSp>>.usb2PosY
  expr: Constraints[25] = <<specificSp>>.usb1PosY
  sketch-geometry (9):
    g0: LineSegment StartX=-21.7 StartY=78.8 StartZ=0 EndX=-8 EndY=78.8 EndZ=0
    g1: LineSegment StartX=-8 StartY=78.8 StartZ=0 EndX=-8 EndY=72.5 EndZ=0
    g2: LineSegment StartX=-8 StartY=72.5 StartZ=0 EndX=-21.7 EndY=72.5 EndZ=0
    g3: LineSegment StartX=-21.7 StartY=72.5 StartZ=0 EndX=-21.7 EndY=78.8 EndZ=0
    g4: LineSegment StartX=-21.7 StartY=61.3 StartZ=0 EndX=-8 EndY=61.3 EndZ=0
    g5: LineSegment StartX=-8 StartY=61.3 StartZ=0 EndX=-8 EndY=55 EndZ=0
    g6: LineSegment StartX=-8 StartY=55 StartZ=0 EndX=-21.7 EndY=55 EndZ=0
    g7: LineSegment StartX=-21.7 StartY=55 StartZ=0 EndX=-21.7 EndY=61.3 EndZ=0
    g8: GeomPoint X=0 Y=20 Z=0
  constraints (26):
    c: Coincident(g0,g1)
    c: Coincident(g1,g2)
    c: Coincident(g2,g3)
    c: Coincident(g3,g0)
    c: Horizontal(g0)
    c: Horizontal(g2)
    c: Vertical(g1)
    c: Vertical(g3)
    c: Coincident(g4,g5)
    c: Coincident(g5,g6)
    c: Coincident(g6,g7)
    c: Coincident(g7,g4)
    c: Horizontal(g4)
    c: Horizontal(g6)
    c: Vertical(g5)
    c: Vertical(g7)
    c: DistanceX(g5,g-1) = 8
    c: Vertical(g1,g4)
    c: Equal(g2,g4)
    c: Equal(g7,g3)
    c: DistanceX(g0,g0) = 13.7
    c: DistanceY(g2,g0) = 6.3
    c: PointOnObject(g8,g-2)
    c: DistanceY(g-1,g8) = 20
    c: DistanceY(g8,g5) = 35
    c: DistanceY(g8,g1) = 52.5
FEATURE [PartDesign::Pocket] Pocket023  label="trousUsb"
  BaseFeature = -> Pocket022
  Direction = (0,0.707107,-0.707107)
  Length = 5
  Length2 = 5
  Profile = -> Sketch048
  ReferenceAxis = -> Sketch048 [N_Axis]
  Type = 0
FEATURE [Sketcher::SketchObject] Sketch049
  FullyConstrained = true
  MapMode = 5
  Placement = pos=(0,0,0) rot=(0.57735,0.57735,0.57735;2.0944rad)
  Support = -> [YZ_Plane003]
  expr: Constraints[12] = <<sp>>.planFaceAvant
  expr: Constraints[15] = <<sp>>.distZeroPlanFAV
  expr: Constraints[16] = <<specificSp>>.usb2PosY + <<specificSp>>.usbFenLarg - 0.6
  expr: Constraints[7] = <<specificSp>>.languetteHaut
  expr: Constraints[8] = <<specificSp>>.languetteLarg
  sketch-geometry (6):
    g0: LineSegment StartX=-41.6655 StartY=51.6188 StartZ=0 EndX=-37.635 EndY=47.5883 EndZ=0
    g1: LineSegment StartX=-37.635 StartY=47.5883 StartZ=0 EndX=-46.3324 EndY=38.8909 EndZ=0
    g2: LineSegment StartX=-46.3324 StartY=38.8909 StartZ=0 EndX=-50.3629 EndY=42.9214 EndZ=0
    g3: LineSegment StartX=-50.3629 StartY=42.9214 StartZ=0 EndX=-41.6655 EndY=51.6188 EndZ=0
    g4: LineSegment StartX=-50.3629 StartY=42.9214 StartZ=0 EndX=-93.2843 EndY=0 EndZ=0
    g5: GeomPoint X=-79.1421 Y=14.1421 Z=0
  constraints (17):
    c: Coincident(g0,g1)
    c: Coincident(g1,g2)
    c: Coincident(g2,g3)
    c: Coincident(g3,g0)
    c: Equal(g0,g2)
    c: Equal(g1,g3)
    c: Perpendicular(g0,g3)
    c: Distance(g0) = 5.7
    c: Distance(g1) = 12.3
    c: Angle(g-1,g1) = 0.785398
    c: Coincident(g4,g2)
    c: PointOnObject(g4,g-1)
    c: DistanceX(g4,g-1) = 93.2843
    c: Angle(g-1,g4) = 0.785398
    c: PointOnObject(g5,g4)
    c: Distance(g4,g5) = 20
    c: Distance(g5,g2) = 40.7
FEATURE [PartDesign::Pocket] Pocket024  label="trouLanguette"
  BaseFeature = -> Pocket023
  Direction = (-1,2e-16,-3e-16)
  Length = 22
  Length2 = 5
  Profile = -> Sketch049
  ReferenceAxis = -> Sketch049 [N_Axis]
  Type = 0
  expr: Length = <<specificSp>>.languetteLong
FEATURE [Sketcher::SketchObject] Sketch050
  FullyConstrained = true
  MapMode = 5
  Placement = pos=(0,0,0) rot=(0.57735,0.57735,0.57735;2.0944rad)
  Support = -> [YZ_Plane003]
  expr: Constraints[10] = <<sp>>.planFaceAvant - <<sp>>.epaisseurParois * sqrt(2)
  expr: Constraints[12] = <<specificSp>>.languetteHaut - <<sp>>.epaisseurParois
  expr: Constraints[14] = <<sp>>.distZeroPlanFAV - <<sp>>.epaisseurParois
  expr: Constraints[15] = <<specificSp>>.usb2PosY + <<specificSp>>.usbFenLarg - 2 - 0.6
  expr: Constraints[16] = <<specificSp>>.languetteLarg + 4
  sketch-geometry (6):
    g0: LineSegment StartX=-50.0093 StartY=39.7394 StartZ=0 EndX=-38.4835 EndY=51.2652 EndZ=0
    g1: LineSegment StartX=-38.4835 StartY=51.2652 StartZ=0 EndX=-36.2208 EndY=49.0025 EndZ=0
    g2: LineSegment StartX=-36.2208 StartY=49.0025 StartZ=0 EndX=-47.7466 EndY=37.4767 EndZ=0
    g3: LineSegment StartX=-47.7466 StartY=37.4767 StartZ=0 EndX=-50.0093 EndY=39.7394 EndZ=0
    g4: LineSegment StartX=-89.7487 StartY=0 StartZ=0 EndX=-50.0093 EndY=39.7394 EndZ=0
    g5: GeomPoint X=-77.3744 Y=12.3744 Z=0
  constraints (17):
    c: Coincident(g0,g1)
    c: Coincident(g1,g2)
    c: Coincident(g2,g3)
    c: Coincident(g3,g0)
    c: Perpendicular(g1,g0)
    c: Parallel(g3,g1)
    c: Parallel(g2,g0)
    c: Angle(g-1,g2) = 0.785398
    c: PointOnObject(g4,g-1)
    c: Coincident(g4,g0)
    c: DistanceX(g4,g-1) = 89.7487
    c: Angle(g-1,g4) = 0.785398
    c: Distance(g1) = 3.2
    c: PointOnObject(g5,g4)
    c: Distance(g5,g4) = 17.5
    c: Distance(g5,g0) = 38.7
    c: Distance(g2) = 16.3
FEATURE [PartDesign::Pocket] Pocket025  label="oreilleLanguette"
  BaseFeature = -> Pocket024
  Direction = (-1,2e-16,-3e-16)
  Length = 5
  Length2 = 5
  Profile = -> Sketch050
  ReferenceAxis = -> Sketch050 [N_Axis]
  Type = 0
FEATURE [PartDesign::Plane] DatumPlane017  label="planFaceAvantFaceInterne"
  AttachmentOffset = pos=(0,0,89.7487) rot=(-1,0,0;0.785398rad)
  Length = 134.936
  MapMode = 5
  Placement = pos=(0,-89.7487,-1.99e-14) rot=(1,0,0;0.785398rad)
  ResizeMode = 0
  Support = -> [XZ_Plane003]
  Width = 166.253
  expr: .AttachmentOffset.Base.z = <<sp>>.planFaceAvant - <<sp>>.epaisseurParois * sqrt(2)
FEATURE [Sketcher::SketchObject] Sketch051  label="evidementSwitchSk"
  FullyConstrained = true
  MapMode = 5
  Placement = pos=(0,-89.7487,-2.13e-14) rot=(0,0.92388,0.382683;3.14159rad)
  Support = -> [DatumPlane017]
  expr: Constraints[10] = <<specificSp>>.switch1PosX - 1
  expr: Constraints[11] = <<specificSp>>.switch2PosY + <<sp>>.distZeroPlanFAV - <<sp>>.epaisseurParois - 2
  expr: Constraints[13] = <<sp>>.distZeroPlanFAV - <<sp>>.epaisseurParois
  expr: Constraints[8] = <<specificSp>>.switchTrouLong * 2 + <<specificSp>>.switchDistY + 4
  expr: Constraints[9] = <<specificSp>>.switchTrouLarg + 2
  sketch-geometry (5):
    g0: LineSegment StartX=25 StartY=81.5 StartZ=0 EndX=35.8 EndY=81.5 EndZ=0
    g1: LineSegment StartX=35.8 StartY=81.5 StartZ=0 EndX=35.8 EndY=45.5 EndZ=0
    g2: LineSegment StartX=35.8 StartY=45.5 StartZ=0 EndX=25 EndY=45.5 EndZ=0
    g3: LineSegment StartX=25 StartY=45.5 StartZ=0 EndX=25 EndY=81.5 EndZ=0
    g4: GeomPoint X=0 Y=17.5 Z=0
  constraints (14):
    c: Coincident(g0,g1)
    c: Coincident(g1,g2)
    c: Coincident(g2,g3)
    c: Coincident(g3,g0)
    c: Horizontal(g0)
    c: Horizontal(g2)
    c: Vertical(g1)
    c: Vertical(g3)
    c: DistanceY(g3,g3) = 36
    c: DistanceX(g2,g2) = 10.8
    c: DistanceX(g-1,g2) = 25
    c: DistanceY(g-1,g2) = 45.5
    c: PointOnObject(g4,g-2)
    c: DistanceY(g-1,g4) = 17.5
FEATURE [PartDesign::Pocket] Pocket026  label="evidementSwitch"
  BaseFeature = -> Pocket025
  Direction = (0,-0.707107,0.707107)
  Length = 2
  Length2 = 5
  Profile = -> Sketch051
  ReferenceAxis = -> Sketch051 [N_Axis]
  Type = 0
FEATURE [Sketcher::SketchObject] Sketch052
  FullyConstrained = true
  MapMode = 5
  Placement = pos=(0,-89.7487,-2.13e-14) rot=(0,0.92388,0.382683;3.14159rad)
  Support = -> [DatumPlane017]
  expr: Constraints[10] = <<specificSp>>.usb2PosY
  expr: Constraints[11] = <<specificSp>>.usb1PosX
  expr: Constraints[12] = <<specificSp>>.usbFenLong
  expr: Constraints[9] = <<sp>>.distZeroPlanFAV - <<sp>>.epaisseurParois
  sketch-geometry (5):
    g0: LineSegment StartX=8 StartY=52.5 StartZ=0 EndX=21.7 EndY=52.5 EndZ=0
    g1: LineSegment StartX=21.7 StartY=52.5 StartZ=0 EndX=21.7 EndY=48.5 EndZ=0
    g2: LineSegment StartX=21.7 StartY=48.5 StartZ=0 EndX=8 EndY=48.5 EndZ=0
    g3: LineSegment StartX=8 StartY=48.5 StartZ=0 EndX=8 EndY=52.5 EndZ=0
    g4: GeomPoint X=0 Y=17.5 Z=0
  constraints (14):
    c: Coincident(g0,g1)
    c: Coincident(g1,g2)
    c: Coincident(g2,g3)
    c: Coincident(g3,g0)
    c: Horizontal(g0)
    c: Horizontal(g2)
    c: Vertical(g1)
    c: Vertical(g3)
    c: PointOnObject(g4,g-2)
    c: DistanceY(g-1,g4) = 17.5
    c: DistanceY(g4,g0) = 35
    c: DistanceX(g4,g2) = 8
    c: DistanceX(g2,g1) = 13.7
    c: DistanceY(g1,g1) = 4
FEATURE [PartDesign::Pad] Pad026  label="plotUsb2"
  BaseFeature = -> Pocket026
  Direction = (0,0.707107,-0.707107)
  Length = 3.2
  Length2 = 10
  Profile = -> Sketch052
  ReferenceAxis = -> Sketch052 [N_Axis]
  Type = 0
FEATURE [Sketcher::SketchObject] Sketch057  label="pcbplotSk"
  FullyConstrained = true
  MapMode = 5
  Placement = pos=(0,-89.7487,-2.13e-14) rot=(1,0,0;0.785398rad)
  Support = -> [DatumPlane017]
  expr: Constraints[19] = <<specificSp>>.pcbPlotTaille
  expr: Constraints[21] = <<sp>>.distZeroPlanFAV - <<sp>>.epaisseurParois
  expr: Constraints[22] = <<specificSp>>.pcbPosX
  expr: Constraints[23] = <<specificSp>>.pcbPosY
  expr: Constraints[26] = <<specificSp>>.pcbtrousDx
  expr: Constraints[27] = <<specificSp>>.pcbTrousDy
  sketch-geometry (13):
    g0: LineSegment StartX=-52.6 StartY=93.84 StartZ=0 EndX=-52.6 EndY=87.84 EndZ=0
    g1: LineSegment StartX=-52.6 StartY=87.84 StartZ=0 EndX=-46.6 EndY=87.84 EndZ=0
    g2: LineSegment StartX=-46.6 StartY=87.84 StartZ=0 EndX=-46.6 EndY=93.84 EndZ=0
    g3: LineSegment StartX=-46.6 StartY=93.84 StartZ=0 EndX=-52.6 EndY=93.84 EndZ=0
    g4: GeomPoint X=-49.6 Y=90.84 Z=0
    g5: LineSegment StartX=-78 StartY=40.5 StartZ=0 EndX=-78 EndY=34.5 EndZ=0
    g6: LineSegment StartX=-78 StartY=34.5 StartZ=0 EndX=-72 EndY=34.5 EndZ=0
    g7: LineSegment StartX=-72 StartY=34.5 StartZ=0 EndX=-72 EndY=40.5 EndZ=0
    g8: LineSegment StartX=-72 StartY=40.5 StartZ=0 EndX=-78 EndY=40.5 EndZ=0
    g9: GeomPoint X=-75 Y=37.5 Z=0
    g10: GeomPoint X=0 Y=17.5 Z=0
    g11: Circle CenterX=-49.6 CenterY=90.84 CenterZ=0 NormalX=0 NormalY=0 NormalZ=1 AngleXU=0 Radius=2
    g12: Circle CenterX=-75 CenterY=37.5 CenterZ=0 NormalX=0 NormalY=0 NormalZ=1 AngleXU=0 Radius=2
  constraints (32):
    c: Coincident(g0,g1)
    c: Coincident(g1,g2)
    c: Coincident(g2,g3)
    c: Coincident(g3,g0)
    c: Horizontal(g1)
    c: Horizontal(g3)
    c: Vertical(g0)
    c: Vertical(g2)
    c: Symmetric(g1,g0,g4)
    c: Coincident(g5,g6)
    c: Coincident(g6,g7)
    c: Coincident(g7,g8)
    c: Coincident(g8,g5)
    c: Horizontal(g6)
    c: Horizontal(g8)
    c: Vertical(g5)
    c: Vertical(g7)
    c: Symmetric(g6,g5,g9)
    c: Equal(g6,g7)
    c: DistanceX(g5,g6) = 6
    c: PointOnObject(g10,g-2)
    c: DistanceY(g-1,g10) = 17.5
    c: DistanceX(g9,g10) = 75
    c: DistanceY(g10,g9) = 20
    c: Equal(g1,g2)
    c: Equal(g2,g6)
    c: DistanceX(g9,g4) = 25.4
    c: DistanceY(g9,g4) = 53.34
    c: Coincident(g11,g4)
    c: Coincident(g12,g9)
    c: Equal(g12,g11)
    c: Diameter(g12) = 4
FEATURE [PartDesign::Pad] Pad029  label="pcbPlotPad"
  BaseFeature = -> Pad026
  Direction = (0,-0.707107,0.707107)
  Length = 6.06
  Length2 = 10
  Profile = -> Sketch057
  ReferenceAxis = -> Sketch057 [N_Axis]
  Reversed = true
  Type = 0
  expr: Length = <<specificSp>>.pcbPlotHaut
FEATURE [Sketcher::SketchObject] Sketch058
  FullyConstrained = true
  MapMode = 5
  Placement = pos=(0,-93.2843,-2.84e-14) rot=(1,0,0;0.785398rad)
  Support = -> [DatumPlane011]
  expr: Constraints[10] = <<specificSp>>.pcbPosX
  expr: Constraints[11] = <<specificSp>>.pcbPosY
  expr: Constraints[13] = <<specificSp>>.oledDisYvsOPvb
  expr: Constraints[14] = <<specificSp>>.oledDx
  expr: Constraints[15] = <<specificSp>>.oledDy
  expr: Constraints[16] = <<specificSp>>.oledFanLong
  expr: Constraints[17] = <<specificSp>>.oledFenLarg
  expr: Constraints[9] = <<sp>>.distZeroPlanFAV
  sketch-geometry (7):
    g0: LineSegment StartX=-71.1 StartY=69.72 StartZ=0 EndX=-44.6 EndY=69.72 EndZ=0
    g1: LineSegment StartX=-44.6 StartY=69.72 StartZ=0 EndX=-44.6 EndY=58.22 EndZ=0
    g2: LineSegment StartX=-44.6 StartY=58.22 StartZ=0 EndX=-71.1 EndY=58.22 EndZ=0
    g3: LineSegment StartX=-71.1 StartY=58.22 StartZ=0 EndX=-71.1 EndY=69.72 EndZ=0
    g4: GeomPoint X=0 Y=20 Z=0
    g5: GeomPoint X=-75 Y=40 Z=0
    g6: GeomPoint X=-75 Y=60.32 Z=0
  constraints (18):
    c: Coincident(g0,g1)
    c: Coincident(g1,g2)
    c: Coincident(g2,g3)
    c: Coincident(g3,g0)
    c: Horizontal(g0)
    c: Horizontal(g2)
    c: Vertical(g1)
    c: Vertical(g3)
    c: PointOnObject(g4,g-2)
    c: DistanceY(g-1,g4) = 20
    c: DistanceX(g5,g4) = 75
    c: DistanceY(g4,g5) = 20
    c: Vertical(g5,g6)
    c: DistanceY(g5,g6) = 20.32
    c: DistanceX(g6,g2) = 3.9
    c: DistanceY(g2,g6) = 2.1
    c: DistanceX(g2,g1) = 26.5
    c: DistanceY(g2,g0) = 11.5
FEATURE [PartDesign::Pocket] Pocket029  label="fenPcb"
  BaseFeature = -> Pad029
  Direction = (0,0.707107,-0.707107)
  Length = 2.5
  Length2 = 5
  Profile = -> Sketch058
  ReferenceAxis = -> Sketch058 [N_Axis]
  Type = 0
  expr: Length = <<sp>>.epaisseurParois
FEATURE [Sketcher::SketchObject] Sketch059
  FullyConstrained = true
  MapMode = 5
  Placement = pos=(0,-89.7487,-2.13e-14) rot=(1,0,0;0.785398rad)
  Support = -> [DatumPlane017]
  expr: Constraints[12] = <<specificSp>>.oledDisYvsOPvb
  expr: Constraints[13] = <<specificSp>>.pcbPosX
  expr: Constraints[14] = <<specificSp>>.pcbPosY
  expr: Constraints[15] = <<sp>>.distZeroPlanFAV - <<sp>>.epaisseurParois
  expr: Constraints[16] = <<specificSp>>.oledPcbDy
  expr: Constraints[17] = <<specificSp>>.oledPcbDx
  expr: Constraints[8] = <<specificSp>>.oledPcbLong + 1
  expr: Constraints[9] = <<specificSp>>.oledPcbLarg + 1
  sketch-geometry (7):
    g0: LineSegment StartX=-76.4 StartY=68.12 StartZ=0 EndX=-37.4 EndY=68.12 EndZ=0
    g1: LineSegment StartX=-37.4 StartY=68.12 StartZ=0 EndX=-37.4 EndY=55.12 EndZ=0
    g2: LineSegment StartX=-37.4 StartY=55.12 StartZ=0 EndX=-76.4 EndY=55.12 EndZ=0
    g3: LineSegment StartX=-76.4 StartY=55.12 StartZ=0 EndX=-76.4 EndY=68.12 EndZ=0
    g4: GeomPoint X=0 Y=17.5 Z=0
    g5: GeomPoint X=-75 Y=37.5 Z=0
    g6: GeomPoint X=-75 Y=57.82 Z=0
  constraints (18):
    c: Coincident(g0,g1)
    c: Coincident(g1,g2)
    c: Coincident(g2,g3)
    c: Coincident(g3,g0)
    c: Horizontal(g0)
    c: Horizontal(g2)
    c: Vertical(g1)
    c: Vertical(g3)
    c: DistanceX(g2,g2) = 39
    c: DistanceY(g1,g1) = 13
    c: PointOnObject(g4,g-2)
    c: Vertical(g6,g5)
    c: DistanceY(g5,g6) = 20.32
    c: DistanceX(g5,g4) = 75
    c: DistanceY(g4,g5) = 20
    c: DistanceY(g-1,g4) = 17.5
    c: DistanceY(g2,g6) = 2.7
    c: DistanceX(g2,g6) = 1.4
FEATURE [PartDesign::Pocket] Pocket030  label="emprunteOled"
  BaseFeature = -> Pocket029
  Direction = (0,0.707107,-0.707107)
  Length = 1.9
  Length2 = 5
  Profile = -> Sketch059
  ReferenceAxis = -> Sketch059 [N_Axis]
  Reversed = true
  Type = 0
  expr: Length = <<sp>>.epaisseurParois - 0.6
FEATURE [PartDesign::Plane] DatumPlane018
  AttachmentOffset = pos=(0,0,65) rot=(1,0,0;0.785398rad)
  Length = 134.936
  MapMode = 5
  Placement = pos=(0,-65,-1.44e-14) rot=(1,0,0;2.35619rad)
  ResizeMode = 0
  Support = -> [XZ_Plane003]
  Width = 166.253
  expr: .AttachmentOffset.Base.z = <<sp>>.Base
  expr: .AttachmentOffset.Rotation.Roll = <<sp>>.anglePetitRetourBase - 90
FEATURE [PartDesign::Body] Body002  label="faceAvant"
  BaseFeature = -> Slice_child1
  Group = -> [Clone001,Thickness001,DatumPlane007,Sketch016,Pad005,Sketch017,Pad006,Sketch018,Pocket010,DatumPlane011,Sketch030,Pad014,Pad015,Sketch031,Pad016,Sketch039,Pocket018,DatumPlane016,Sketch044,Sketch047,Pocket022,Sketch048,Pocket023,Sketch049,Pocket024,Sketch050,Pocket025,DatumPlane017,Sketch051,Pocket026,Sketch052,Pad026,Sketch057,Pad029,Sketch058,Pocket029,Sketch059,Pocket030,DatumPlane018,+2 more]
  Origin = -> Origin003
  Tip = -> Pocket031
COMPONENT P2 — geometry summary ("theBoard"; no construction recipe available for this part):
  bounding box: 59.2 x 55.2 x 51.3 mm
  tessellated surface: 90,692 triangles
  volume: 9571 mm^3 (6% of its bounding box)
COMPONENT P3 — recipe-attached ("ventilo40mm", modeled in this document).
Construction recipe (the document's own serialized feature program — sketch geometry with constraints, then the solid features built on it; lengths are millimeters unless a unit is written):

FEATURE [Sketcher::SketchObject] Sketch  label="profileDeBase"
  FullyConstrained = true
  MapMode = 5
  Placement = pos=(0,0,0) rot=(0.57735,0.57735,0.57735;2.0944rad)
  Support = -> [YZ_Plane001]
  expr: Constraints[10] = <<sp>>.petitRetour
  expr: Constraints[11] = <<sp>>.angleFacePetitRetour
  expr: Constraints[12] = <<sp>>.Face
  expr: Constraints[13] = <<sp>>.angleFaceRetourHaut
  expr: Constraints[8] = <<sp>>.Base
  expr: Constraints[9] = <<sp>>.anglePetitRetourBase
  sketch-geometry (5):
    g0: LineSegment StartX=0 StartY=0 StartZ=0 EndX=-65 EndY=0 EndZ=0
    g1: LineSegment StartX=-65 StartY=0 StartZ=0 EndX=-79.1421 EndY=14.1421 EndZ=0
    g2: LineSegment StartX=-79.1421 StartY=14.1421 StartZ=0 EndX=-22.5736 EndY=70.7107 EndZ=0
    g3: LineSegment StartX=-22.5736 StartY=70.7107 StartZ=0 EndX=0 EndY=48.1371 EndZ=0
    g4: LineSegment StartX=0 StartY=48.1371 StartZ=0 EndX=0 EndY=0 EndZ=0
  constraints (14):
    c: Coincident(g-1,g0)
    c: Horizontal(g0)
    c: Coincident(g0,g1)
    c: Coincident(g1,g2)
    c: Coincident(g2,g3)
    c: PointOnObject(g3,g-2)
    c: Coincident(g3,g4)
    c: Coincident(g4,g0)
    c: DistanceX(g0,g0) = 65
    c: Angle(g0,g1) = 2.35619
    c: Distance(g1) = 20
    c: Angle(g1,g2) = 1.5708
    c: Distance(g2) = 80
    c: Angle(g2,g3) = 1.5708
FEATURE [PartDesign::Pad] Pad
  AllowMultiFace = false
  Direction = (1,-2e-16,3e-16)
  Length = 85
  Length2 = 100
  Placement = pos=(0,0,0) rot=(0.57735,0.57735,0.57735;2.0944rad)
  Profile = -> Sketch
  Reversed = true
  Type = 0
  expr: Length = <<sp>>.largeurModuleBase
FEATURE [PartDesign::Plane] DatumPlane
  AttachmentOffset = pos=(71,0,0) rot=(0,-1,0;0.785398rad)
  Length = 98.6412
  MapMode = 5
  Placement = pos=(-7.9e-15,8e-15,71) rot=(0.678598,0.678598,0.281085;3.68962rad)
  ResizeMode = 0
  Support = -> [Pad]
  Width = 63.0813
FEATURE [PartDesign::Body] Body  label="Base"
  Group = -> [Sketch,Pad,DatumPlane]
  Origin = -> Origin001
  Tip = -> Pad
COMPONENT P4 — geometry summary ("usbFem001"; no construction recipe available for this part):
  bounding box: 22.8 x 17.0 x 15.8 mm
  tessellated surface: 87,732 triangles
  volume: 995 mm^3 (16% of its bounding box)
  symmetry: mirror-symmetric across its x mid-plane
COMPONENT P5 — geometry summary ("switch_002"; no construction recipe available for this part):
  bounding box: 19.2 x 16.9 x 10.5 mm
  tessellated surface: 276 triangles
  volume: 1181 mm^3 (35% of its bounding box)
  symmetry: mirror-symmetric across its x mid-plane
COMPONENT P6 — geometry summary ("trimmer002"; no construction recipe available for this part):
  bounding box: 11.0 x 9.6 x 9.3 mm
  tessellated surface: 2,090 triangles
  volume: 357 mm^3 (36% of its bounding box)
COMPONENT P7 — recipe-attached ("languetteFavPrt001", modeled in this document).
Construction recipe (the document's own serialized feature program — sketch geometry with constraints, then the solid features built on it; lengths are millimeters unless a unit is written):

FEATURE [Sketcher::SketchObject] Sketch053
  FullyConstrained = true
  MapMode = 5
  Placement = pos=(0,0,0) rot=(0.57735,0.57735,0.57735;2.0944rad)
  Support = -> [YZ_Plane026]
  expr: Constraints[8] = <<specificSp>>.languetteLarg - Spreadsheet002.jeuLang
  expr: Constraints[9] = <<specificSp>>.languetteHaut - Spreadsheet002.jeuLang
  sketch-geometry (4):
    g0: LineSegment StartX=-5.9 StartY=0 StartZ=0 EndX=5.9 EndY=0 EndZ=0
    g1: LineSegment StartX=5.9 StartY=0 StartZ=0 EndX=5.9 EndY=5.2 EndZ=0
    g2: LineSegment StartX=5.9 StartY=5.2 StartZ=0 EndX=-5.9 EndY=5.2 EndZ=0
    g3: LineSegment StartX=-5.9 StartY=5.2 StartZ=0 EndX=-5.9 EndY=0 EndZ=0
  constraints (11):
    c: Coincident(g0,g1)
    c: Coincident(g1,g2)
    c: Coincident(g2,g3)
    c: Coincident(g3,g0)
    c: Horizontal(g2)
    c: Vertical(g1)
    c: Vertical(g3)
    c: PointOnObject(g0,g-1)
    c: DistanceX(g2,g2) = 11.8
    c: DistanceY(g0,g1) = 5.2
    c: Symmetric(g0,g0,g-2)
FEATURE [PartDesign::Pad] Pad027  label="extrusionPrincipale"
  Direction = (1,-2e-16,3e-16)
  Length = 24
  Length2 = 10
  Placement = pos=(0,0,0) rot=(0.57735,0.57735,0.57735;2.0944rad)
  Profile = -> Sketch053
  ReferenceAxis = -> Sketch053 [N_Axis]
  Reversed = true
  Type = 0
  expr: Length = <<specificSp>>.languetteLong + 2
FEATURE [Sketcher::SketchObject] Sketch054
  FullyConstrained = true
  MapMode = 5
  Placement = pos=(0,0,0) rot=(1,0,0;1.5708rad)
  Support = -> [XZ_Plane026]
  expr: Constraints[10] = <<specificSp>>.languetteLong - Spreadsheet002.jeuLang
  expr: Constraints[11] = <<specificSp>>.languetteHaut
  expr: Constraints[8] = 2 + Spreadsheet002.jeuLang
  expr: Constraints[9] = <<sp>>.epaisseurParois + Spreadsheet002.jeuLang
  sketch-geometry (4):
    g0: LineSegment StartX=-24 StartY=5.7 StartZ=0 EndX=-21.5 EndY=5.7 EndZ=0
    g1: LineSegment StartX=-21.5 StartY=5.7 StartZ=0 EndX=-21.5 EndY=2.7 EndZ=0
    g2: LineSegment StartX=-21.5 StartY=2.7 StartZ=0 EndX=-24 EndY=2.7 EndZ=0
    g3: LineSegment StartX=-24 StartY=2.7 StartZ=0 EndX=-24 EndY=5.7 EndZ=0
  constraints (12):
    c: Coincident(g0,g1)
    c: Coincident(g1,g2)
    c: Coincident(g2,g3)
    c: Coincident(g3,g0)
    c: Horizontal(g0)
    c: Horizontal(g2)
    c: Vertical(g1)
    c: Vertical(g3)
    c: DistanceX(g0,g0) = 2.5
    c: DistanceY(g3,g3) = 3
    c: DistanceX(g1,g-1) = 21.5
    c: DistanceY(g-1,g0) = 5.7
FEATURE [PartDesign::Pocket] Pocket027  label="edidement"
  BaseFeature = -> Pad027
  Direction = (0,1,2e-16)
  Length = 12.3
  Length2 = 5
  Midplane = true
  Placement = pos=(0,0,0) rot=(0.57735,0.57735,0.57735;2.0944rad)
  Profile = -> Sketch054
  ReferenceAxis = -> Sketch054 [N_Axis]
  Type = 0
  expr: Length = <<specificSp>>.languetteLarg
FEATURE [Sketcher::SketchObject] Sketch055
  FullyConstrained = true
  MapMode = 5
  Placement = pos=(0,0,0) rot=(0.57735,0.57735,0.57735;2.0944rad)
  Support = -> [YZ_Plane026]
  expr: Constraints[10] = <<specificSp>>.languetteHaut - <<sp>>.epaisseurParois - <<specificSp>>.jeuLang
  expr: Constraints[9] = <<specificSp>>.languetteLarg + 4 - <<specificSp>>.jeuLang
  sketch-geometry (4):
    g0: LineSegment StartX=-7.9 StartY=0 StartZ=0 EndX=7.9 EndY=0 EndZ=0
    g1: LineSegment StartX=7.9 StartY=0 StartZ=0 EndX=7.9 EndY=2.7 EndZ=0
    g2: LineSegment StartX=7.9 StartY=2.7 StartZ=0 EndX=-7.9 EndY=2.7 EndZ=0
    g3: LineSegment StartX=-7.9 StartY=2.7 StartZ=0 EndX=-7.9 EndY=0 EndZ=0
  constraints (11):
    c: Coincident(g0,g1)
    c: Coincident(g1,g2)
    c: Coincident(g2,g3)
    c: Coincident(g3,g0)
    c: Horizontal(g2)
    c: Vertical(g1)
    c: Vertical(g3)
    c: PointOnObject(g0,g-1)
    c: Symmetric(g0,g0,g-2)
    c: DistanceX(g0,g0) = 15.8
    c: DistanceY(g1,g1) = 2.7
FEATURE [PartDesign::Pad] Pad028  label="oreilles"
  BaseFeature = -> Pocket027
  Direction = (1,-2e-16,3e-16)
  Length = 4
  Length2 = 10
  Placement = pos=(0,0,0) rot=(0.57735,0.57735,0.57735;2.0944rad)
  Profile = -> Sketch055
  ReferenceAxis = -> Sketch055 [N_Axis]
  Reversed = true
  Type = 0
  expr: Length = <<sp>>.epaisseurParois + <<sp>>.favEpBordure
FEATURE [Sketcher::SketchObject] Sketch056
  FullyConstrained = true
  MapMode = 5
  Support = -> [XY_Plane026]
  expr: Constraints[2] = <<sp>>.epaisseurParois + <<sp>>.favEpBordure + <<specificSp>>.tetevisM3Diam / 2
  sketch-geometry (1):
    g0: Circle CenterX=-6.75 CenterY=0 CenterZ=0 NormalX=0 NormalY=0 NormalZ=1 AngleXU=0 Radius=2
  constraints (3):
    c: PointOnObject(g0,g-1)
    c: Diameter(g0) = 4
    c: DistanceX(g0,g-1) = 6.75
FEATURE [PartDesign::Pocket] Pocket028
  BaseFeature = -> Pad028
  Direction = (0,0,-1)
  Length = 5
  Length2 = 5
  Placement = pos=(0,0,0) rot=(0.57735,0.57735,0.57735;2.0944rad)
  Profile = -> Sketch056
  ReferenceAxis = -> Sketch056 [N_Axis]
  Reversed = true
  Type = 1
FEATURE [PartDesign::Fillet] Fillet
  Base = -> Pocket028 [Edge11,Edge12,Edge16,Edge43,Edge45,Edge17,Edge9,Edge26,Edge25,Edge35,Edge10,Edge34]
  BaseFeature = -> Pocket028
  Placement = pos=(0,0,0) rot=(0.57735,0.57735,0.57735;2.0944rad)
  Radius = 0.5
  SupportTransform = false
  UseAllEdges = false
FEATURE [PartDesign::Body] Body012  label="languetteFavBdy"
  Group = -> [Sketch053,Pad027,Sketch054,Pocket027,Sketch055,Pad028,Sketch056,Pocket028,Fillet]
  Origin = -> Origin030
  Tip = -> Fillet
COMPONENT P8 — recipe-attached ("visTHCM3x6_FAV003", modeled in this document).
Construction recipe (the document's own serialized feature program — sketch geometry with constraints, then the solid features built on it; lengths are millimeters unless a unit is written):

FEATURE [Sketcher::SketchObject] Sketch034  label="Sketch"
  FullyConstrained = false
  MapMode = 5
  Support = -> [XY_Plane015]
  sketch-geometry (1):
    g0: Circle CenterX=0 CenterY=0 CenterZ=0 NormalX=0 NormalY=0 NormalZ=1 AngleXU=0 Radius=2.75
  constraints (2):
    c: Coincident(g0,g-1)
    c: Diameter(g0) = 5.5
FEATURE [PartDesign::Pad] Pad019  label="tete"
  AllowMultiFace = false
  Direction = (1,1,1)
  Length = 3
  Length2 = 100
  Profile = -> Sketch034
  Type = 0
FEATURE [Sketcher::SketchObject] Sketch001
  FullyConstrained = false
  MapMode = 5
  Placement = pos=(0,0,0) rot=(1,0,0;3.14159rad)
  Support = -> [Pad019]
  sketch-geometry (1):
    g0: Circle CenterX=0 CenterY=0 CenterZ=0 NormalX=0 NormalY=0 NormalZ=1 AngleXU=0 Radius=1.5
  constraints (2):
    c: Coincident(g0,g-1)
    c: Diameter(g0) = 3
FEATURE [PartDesign::Pad] Pad020  label="corps"
  AllowMultiFace = false
  BaseFeature = -> Pad019
  Direction = (1,1,1)
  Length = 6
  Length2 = 100
  Profile = -> Sketch001
  Type = 0
FEATURE [PartDesign::Plane] DatumPlane014
  AttachmentOffset = pos=(0,0,3) rot=(0,0,1;0rad)
  Length = 60
  MapMode = 5
  Placement = pos=(0,0,3) rot=(0,0,1;0rad)
  ResizeMode = 0
  Support = -> [XY_Plane015]
  Width = 60
FEATURE [Sketcher::SketchObject] Sketch035  label="Sketch002"
  FullyConstrained = false
  MapMode = 5
  Placement = pos=(0,0,3) rot=(0,0,1;0rad)
  Support = -> [DatumPlane014]
  sketch-geometry (7):
    g0: LineSegment StartX=0.721688 StartY=-1.25 StartZ=0 EndX=1.44338 EndY=1.0119e-12 EndZ=0
    g1: LineSegment StartX=1.44338 StartY=1.0119e-12 StartZ=0 EndX=0.721688 EndY=1.25 EndZ=0
    g2: LineSegment StartX=0.721688 StartY=1.25 StartZ=0 EndX=-0.721688 EndY=1.25 EndZ=0
    g3: LineSegment StartX=-0.721688 StartY=1.25 StartZ=0 EndX=-1.44338 EndY=8.689e-13 EndZ=0
    g4: LineSegment StartX=-1.44338 StartY=8.689e-13 StartZ=0 EndX=-0.721688 EndY=-1.25 EndZ=0
    g5: LineSegment StartX=-0.721688 StartY=-1.25 StartZ=0 EndX=0.721688 EndY=-1.25 EndZ=0
    g6: Circle CenterX=0 CenterY=0 CenterZ=0 NormalX=0 NormalY=0 NormalZ=1 AngleXU=0 Radius=1.44338
  constraints (16):
    c: Coincident(g0,g1)
    c: Coincident(g1,g2)
    c: Coincident(g2,g3)
    c: Coincident(g3,g4)
    c: Coincident(g4,g5)
    c: Coincident(g5,g0)
    c: Equal(g0, g1-g5) x5
    c: PointOnObject(g0,g6)
    c: PointOnObject(g1,g6)
    c: PointOnObject(g2,g6)
    c: PointOnObject(g3,g6)
    c: PointOnObject(g4,g6)
    c: PointOnObject(g5,g6)
    c: Coincident(g6,g-1)
    c: Horizontal(g2)
    c: DistanceY(g0,g1) = 2.5
FEATURE [PartDesign::Pocket] Pocket016  label="emprunte"
  AllowMultiFace = false
  BaseFeature = -> Pad020
  Direction = (1,1,1)
  Length = 4
  Length2 = 100
  Profile = -> Sketch035
  Type = 0
FEATURE [PartDesign::Body] Body009  label="visTHCM3x6_FAV001"
  Group = -> [Sketch034,Pad019,Sketch001,Pad020,DatumPlane014,Sketch035,Pocket016]
  Origin = -> Origin019
  Placement = pos=(-6.5,-61.8718,6.01041) rot=(1,0,0;3.92699rad)
  Tip = -> Pocket016
COMPONENT P9 — recipe-attached ("7805dissip", modeled in this document).
Construction recipe (the document's own serialized feature program — sketch geometry with constraints, then the solid features built on it; lengths are millimeters unless a unit is written):

FEATURE [Sketcher::SketchObject] Sketch066
  FullyConstrained = true
  MapMode = 5
  Placement = pos=(0,0,0) rot=(1,0,0;1.5708rad)
  Support = -> [XZ_Plane039]
  sketch-geometry (16):
    g0: LineSegment StartX=-5.7 StartY=0 StartZ=0 EndX=5.7 EndY=0 EndZ=0
    g1: LineSegment StartX=5.7 StartY=0 StartZ=0 EndX=5.7 EndY=5.09 EndZ=0
    g2: LineSegment StartX=5.7 StartY=5.09 StartZ=0 EndX=4.56 EndY=5.09 EndZ=0
    g3: LineSegment StartX=4.56 StartY=5.09 StartZ=0 EndX=4.56 EndY=1.15 EndZ=0
    g4: LineSegment StartX=4.56 StartY=1.15 StartZ=0 EndX=2.29 EndY=1.15 EndZ=0
    g5: LineSegment StartX=2.29 StartY=1.15 StartZ=0 EndX=2.29 EndY=5.09 EndZ=0
    g6: LineSegment StartX=2.29 StartY=5.09 StartZ=0 EndX=1.15 EndY=5.09 EndZ=0
    g7: LineSegment StartX=1.15 StartY=5.09 StartZ=0 EndX=1.15 EndY=1.15 EndZ=0
    g8: LineSegment StartX=1.15 StartY=1.15 StartZ=0 EndX=-1.15 EndY=1.15 EndZ=0
    g9: LineSegment StartX=-1.15 StartY=1.15 StartZ=0 EndX=-1.15 EndY=5.09 EndZ=0
    g10: LineSegment StartX=-1.15 StartY=5.09 StartZ=0 EndX=-2.29 EndY=5.09 EndZ=0
    g11: LineSegment StartX=-2.29 StartY=5.09 StartZ=0 EndX=-2.29 EndY=1.15 EndZ=0
    g12: LineSegment StartX=-2.29 StartY=1.15 StartZ=0 EndX=-4.56 EndY=1.15 EndZ=0
    g13: LineSegment StartX=-4.56 StartY=1.15 StartZ=0 EndX=-4.56 EndY=5.09 EndZ=0
    g14: LineSegment StartX=-4.56 StartY=5.09 StartZ=0 EndX=-5.7 EndY=5.09 EndZ=0
    g15: LineSegment StartX=-5.7 StartY=5.09 StartZ=0 EndX=-5.7 EndY=0 EndZ=0
  constraints (46):
    c: PointOnObject(g0,g-1)
    c: Coincident(g0,g1)
    c: Vertical(g1)
    c: Coincident(g1,g2)
    c: Horizontal(g2)
    c: Coincident(g2,g3)
    c: Vertical(g3)
    c: Coincident(g3,g4)
    c: Coincident(g4,g5)
    c: Coincident(g5,g6)
    c: Coincident(g6,g7)
    c: Coincident(g7,g8)
    c: Coincident(g8,g9)
    c: Coincident(g9,g10)
    c: Horizontal(g10)
    c: Coincident(g10,g11)
    c: Coincident(g11,g12)
    c: Coincident(g12,g13)
    c: Coincident(g13,g14)
    c: Coincident(g14,g15)
    c: Coincident(g0,g15)
    c: Vertical(g15)
    c: Symmetric(g0,g0,g-2)
    c: Horizontal(g6)
    c: Horizontal(g4)
    c: Symmetric(g8,g7,g-2)
    c: DistanceX(g0,g0) = 11.4
    c: Vertical(g13)
    c: Horizontal(g14)
    c: Horizontal(g12)
    c: Horizontal(g13,g10)
    c: Horizontal(g9,g6)
    c: Vertical(g9)
    c: Vertical(g7)
    c: Vertical(g5)
    c: Horizontal(g5,g2)
    c: Horizontal(g11,g8)
    c: Horizontal(g7,g4)
    c: Vertical(g11)
    c: DistanceX(g2,g2) = 1.14
    c: Equal(g2,g6)
    c: Equal(g6,g10)
    c: Equal(g10,g14)
    c: DistanceX(g4,g4) = 2.27
    c: DistanceY(g0,g1) = 5.09
    c: DistanceY(g0,g12) = 1.15
FEATURE [PartDesign::Pad] Pad035
  Direction = (0,-1,-2e-16)
  Length = 11.13
  Length2 = 10
  Midplane = true
  Placement = pos=(0,0,0) rot=(1,0,0;1.5708rad)
  Profile = -> Sketch066
  ReferenceAxis = -> Sketch066 [N_Axis]
  Type = 0
  expr: Length = Spreadsheet008.Long
FEATURE [PartDesign::Fillet] Fillet006
  Base = -> Pad035 [Edge44,Edge41,Edge32,Edge29,Edge20,Edge17,Edge8,Edge5,Edge38,Edge26,Edge14,Edge35,Edge23,Edge11]
  BaseFeature = -> Pad035
  Placement = pos=(0,0,0) rot=(1,0,0;1.5708rad)
  Radius = 0.4
  SupportTransform = false
  UseAllEdges = false
FEATURE [PartDesign::Body] Body018  label="dissipBdy005"
  Group = -> [Sketch066,Pad035,Fillet006]
  Origin = -> Origin043
  Tip = -> Fillet006
COMPONENT P10 — recipe-attached ("tigeLaiton001", modeled in this document).
Construction recipe (the document's own serialized feature program — sketch geometry with constraints, then the solid features built on it; lengths are millimeters unless a unit is written):

FEATURE [PartDesign::Plane] DatumPlane012  label="planBaseTige"
  AttachmentOffset = pos=(0,0,-5.18) rot=(0,0,1;0rad)
  Length = 60
  MapMode = 5
  Placement = pos=(-5.18,1.2e-15,-1.2e-15) rot=(0.57735,0.57735,0.57735;2.0944rad)
  ResizeMode = 0
  Support = -> [YZ_Plane012]
  Width = 60
  expr: .AttachmentOffset.Base.z = -<<tige>>.planBaseTigeposX
FEATURE [Sketcher::SketchObject] Sketch032  label="sk_tiges"
  FullyConstrained = true
  MapMode = 5
  Placement = pos=(-5.18,1.2e-15,-1.2e-15) rot=(0.57735,0.57735,0.57735;2.0944rad)
  Support = -> [DatumPlane012]
  expr: Constraints[0] = <<tige>>.tigeDiam
  expr: Constraints[1] = <<tige>>.tigePosY
  expr: Constraints[2] = <<tige>>.tigePosX
  sketch-geometry (1):
    g0: Circle CenterX=-14 CenterY=14.3 CenterZ=0 NormalX=0 NormalY=0 NormalZ=1 AngleXU=0 Radius=1.25
  constraints (3):
    c: Diameter(g0) = 2.5
    c: DistanceY(g-1,g0) = 14.3
    c: DistanceX(g0,g-1) = 14
FEATURE [PartDesign::Pad] Pad017  label="tigeBasse"
  AllowMultiFace = false
  Direction = (1,-1e-16,1e-16)
  Length = 68.62
  Length2 = 100
  Placement = pos=(-5.18,1e-15,-1e-15) rot=(0.57735,0.57735,0.57735;2.0944rad)
  Profile = -> Sketch032
  Reversed = true
  Type = 0
  expr: Length = <<tige>>.tigeLong
FEATURE [PartDesign::Body] Body007  label="tigeLaiton"
  Group = -> [DatumPlane012,Sketch032,Pad017]
  Origin = -> Origin016
  Tip = -> Pad017
FEATURE [PartDesign::Plane] DatumPlane013  label="planTige2"
  AttachmentOffset = pos=(0,0,-5.18) rot=(0,0,1;0rad)
  Length = 60
  MapMode = 5
  Placement = pos=(-5.18,1.2e-15,-1.2e-15) rot=(0.57735,0.57735,0.57735;2.0944rad)
  ResizeMode = 0
  Support = -> [YZ_Plane014]
  Width = 60
  expr: .AttachmentOffset.Base.z = -<<tige>>.planBaseTigeposX
FEATURE [Sketcher::SketchObject] Sketch033  label="sk_tige2"
  FullyConstrained = true
  MapMode = 5
  Placement = pos=(-5.18,1.2e-15,-1.2e-15) rot=(0.57735,0.57735,0.57735;2.0944rad)
  Support = -> [DatumPlane013]
  expr: Constraints[0] = <<tige>>.tigeDiam
  expr: Constraints[1] = <<tige>>.tigePosX
  expr: Constraints[2] = <<tige>>.tigePosY + <<tige>>.xtEcartBroches
  sketch-geometry (1):
    g0: Circle CenterX=-14 CenterY=21.86 CenterZ=0 NormalX=0 NormalY=0 NormalZ=1 AngleXU=0 Radius=1.25
  constraints (3):
    c: Diameter(g0) = 2.5
    c: DistanceX(g0,g-1) = 14
    c: DistanceY(g-1,g0) = 21.86
FEATURE [PartDesign::Pad] Pad018
  AllowMultiFace = false
  Direction = (1,-1e-16,1e-16)
  Length = 68.62
  Length2 = 100
  Placement = pos=(-5.18,1e-15,-1e-15) rot=(0.57735,0.57735,0.57735;2.0944rad)
  Profile = -> Sketch033
  Reversed = true
  Type = 0
  expr: Length = <<tige>>.tigeLong
FEATURE [PartDesign::Body] Body008  label="tige2"
  Group = -> [DatumPlane013,Sketch033,Pad018]
  Origin = -> Origin018
  Tip = -> Pad018
COMPONENT P11 — geometry summary ("xtVisInsertFix"; no construction recipe available for this part):
  bounding box: 20.2 x 17.7 x 16.6 mm
  tessellated surface: 21,850 triangles
  volume: 1306 mm^3 (22% of its bounding box)
COMPONENT P12 — geometry summary ("xtVisInertMob"; no construction recipe available for this part):
  bounding box: 20.5 x 17.8 x 16.5 mm
  tessellated surface: 32,722 triangles
  volume: 1060 mm^3 (18% of its bounding box)
COMPONENT P13 — recipe-attached ("visInsertFavFix", modeled in this document).
Construction recipe (the document's own serialized feature program — sketch geometry with constraints, then the solid features built on it; lengths are millimeters unless a unit is written):

FEATURE [Sketcher::SketchObject] Sketch034  label="Sketch"
  FullyConstrained = false
  MapMode = 5
  Support = -> [XY_Plane015]
  sketch-geometry (1):
    g0: Circle CenterX=0 CenterY=0 CenterZ=0 NormalX=0 NormalY=0 NormalZ=1 AngleXU=0 Radius=2.75
  constraints (2):
    c: Coincident(g0,g-1)
    c: Diameter(g0) = 5.5
FEATURE [PartDesign::Pad] Pad019  label="tete"
  AllowMultiFace = false
  Direction = (1,1,1)
  Length = 3
  Length2 = 100
  Profile = -> Sketch034
  Type = 0
FEATURE [Sketcher::SketchObject] Sketch001
  FullyConstrained = false
  MapMode = 5
  Placement = pos=(0,0,0) rot=(1,0,0;3.14159rad)
  Support = -> [Pad019]
  sketch-geometry (1):
    g0: Circle CenterX=0 CenterY=0 CenterZ=0 NormalX=0 NormalY=0 NormalZ=1 AngleXU=0 Radius=1.5
  constraints (2):
    c: Coincident(g0,g-1)
    c: Diameter(g0) = 3
FEATURE [PartDesign::Pad] Pad020  label="corps"
  AllowMultiFace = false
  BaseFeature = -> Pad019
  Direction = (1,1,1)
  Length = 6
  Length2 = 100
  Profile = -> Sketch001
  Type = 0
FEATURE [PartDesign::Plane] DatumPlane014
  AttachmentOffset = pos=(0,0,3) rot=(0,0,1;0rad)
  Length = 60
  MapMode = 5
  Placement = pos=(0,0,3) rot=(0,0,1;0rad)
  ResizeMode = 0
  Support = -> [XY_Plane015]
  Width = 60
FEATURE [Sketcher::SketchObject] Sketch035  label="Sketch002"
  FullyConstrained = false
  MapMode = 5
  Placement = pos=(0,0,3) rot=(0,0,1;0rad)
  Support = -> [DatumPlane014]
  sketch-geometry (7):
    g0: LineSegment StartX=0.721688 StartY=-1.25 StartZ=0 EndX=1.44338 EndY=1.0119e-12 EndZ=0
    g1: LineSegment StartX=1.44338 StartY=1.0119e-12 StartZ=0 EndX=0.721688 EndY=1.25 EndZ=0
    g2: LineSegment StartX=0.721688 StartY=1.25 StartZ=0 EndX=-0.721688 EndY=1.25 EndZ=0
    g3: LineSegment StartX=-0.721688 StartY=1.25 StartZ=0 EndX=-1.44338 EndY=8.689e-13 EndZ=0
    g4: LineSegment StartX=-1.44338 StartY=8.689e-13 StartZ=0 EndX=-0.721688 EndY=-1.25 EndZ=0
    g5: LineSegment StartX=-0.721688 StartY=-1.25 StartZ=0 EndX=0.721688 EndY=-1.25 EndZ=0
    g6: Circle CenterX=0 CenterY=0 CenterZ=0 NormalX=0 NormalY=0 NormalZ=1 AngleXU=0 Radius=1.44338
  constraints (16):
    c: Coincident(g0,g1)
    c: Coincident(g1,g2)
    c: Coincident(g2,g3)
    c: Coincident(g3,g4)
    c: Coincident(g4,g5)
    c: Coincident(g5,g0)
    c: Equal(g0, g1-g5) x5
    c: PointOnObject(g0,g6)
    c: PointOnObject(g1,g6)
    c: PointOnObject(g2,g6)
    c: PointOnObject(g3,g6)
    c: PointOnObject(g4,g6)
    c: PointOnObject(g5,g6)
    c: Coincident(g6,g-1)
    c: Horizontal(g2)
    c: DistanceY(g0,g1) = 2.5
FEATURE [PartDesign::Pocket] Pocket016  label="emprunte"
  AllowMultiFace = false
  BaseFeature = -> Pad020
  Direction = (1,1,1)
  Length = 4
  Length2 = 100
  Profile = -> Sketch035
  Type = 0
FEATURE [PartDesign::Body] Body009  label="visTHCM3x6_FAV001"
  Group = -> [Sketch034,Pad019,Sketch001,Pad020,DatumPlane014,Sketch035,Pocket016]
  Origin = -> Origin019
  Placement = pos=(-6.5,-61.8718,6.01041) rot=(1,0,0;3.92699rad)
  Tip = -> Pocket016
COMPONENT P14 — recipe-attached ("visInserFavMob", modeled in this document).
Construction recipe (the document's own serialized feature program — sketch geometry with constraints, then the solid features built on it; lengths are millimeters unless a unit is written):

FEATURE [Sketcher::SketchObject] Sketch036
  FullyConstrained = false
  MapMode = 5
  Support = -> [XY_Plane016]
  sketch-geometry (1):
    g0: Circle CenterX=0 CenterY=0 CenterZ=0 NormalX=0 NormalY=0 NormalZ=1 AngleXU=0 Radius=2.75
  constraints (2):
    c: Coincident(g0,g-1)
    c: Diameter(g0) = 5.5
FEATURE [PartDesign::Pad] Pad021  label="tete001"
  AllowMultiFace = false
  Direction = (1,1,1)
  Length = 3
  Length2 = 100
  Profile = -> Sketch036
  Type = 0
FEATURE [Sketcher::SketchObject] Sketch037
  FullyConstrained = false
  MapMode = 5
  Placement = pos=(0,0,0) rot=(1,0,0;3.14159rad)
  Support = -> [Pad021]
  sketch-geometry (1):
    g0: Circle CenterX=0 CenterY=0 CenterZ=0 NormalX=0 NormalY=0 NormalZ=1 AngleXU=0 Radius=1.5
  constraints (2):
    c: Coincident(g0,g-1)
    c: Diameter(g0) = 3
FEATURE [PartDesign::Pad] Pad022  label="corps001"
  AllowMultiFace = false
  BaseFeature = -> Pad021
  Direction = (1,1,1)
  Length = 6
  Length2 = 100
  Profile = -> Sketch037
  Type = 0
FEATURE [PartDesign::Plane] DatumPlane015
  AttachmentOffset = pos=(0,0,3) rot=(0,0,1;0rad)
  Length = 60
  MapMode = 5
  Placement = pos=(0,0,3) rot=(0,0,1;0rad)
  ResizeMode = 0
  Support = -> [XY_Plane016]
  Width = 60
FEATURE [Sketcher::SketchObject] Sketch038
  FullyConstrained = false
  MapMode = 5
  Placement = pos=(0,0,3) rot=(0,0,1;0rad)
  Support = -> [DatumPlane015]
  sketch-geometry (7):
    g0: LineSegment StartX=0.721688 StartY=-1.25 StartZ=0 EndX=1.44338 EndY=1.0119e-12 EndZ=0
    g1: LineSegment StartX=1.44338 StartY=1.0119e-12 StartZ=0 EndX=0.721688 EndY=1.25 EndZ=0
    g2: LineSegment StartX=0.721688 StartY=1.25 StartZ=0 EndX=-0.721688 EndY=1.25 EndZ=0
    g3: LineSegment StartX=-0.721688 StartY=1.25 StartZ=0 EndX=-1.44338 EndY=8.689e-13 EndZ=0
    g4: LineSegment StartX=-1.44338 StartY=8.689e-13 StartZ=0 EndX=-0.721688 EndY=-1.25 EndZ=0
    g5: LineSegment StartX=-0.721688 StartY=-1.25 StartZ=0 EndX=0.721688 EndY=-1.25 EndZ=0
    g6: Circle CenterX=0 CenterY=0 CenterZ=0 NormalX=0 NormalY=0 NormalZ=1 AngleXU=0 Radius=1.44338
  constraints (16):
    c: Coincident(g0,g1)
    c: Coincident(g1,g2)
    c: Coincident(g2,g3)
    c: Coincident(g3,g4)
    c: Coincident(g4,g5)
    c: Coincident(g5,g0)
    c: Equal(g0, g1-g5) x5
    c: PointOnObject(g0,g6)
    c: PointOnObject(g1,g6)
    c: PointOnObject(g2,g6)
    c: PointOnObject(g3,g6)
    c: PointOnObject(g4,g6)
    c: PointOnObject(g5,g6)
    c: Coincident(g6,g-1)
    c: Horizontal(g2)
    c: DistanceY(g0,g1) = 2.5
FEATURE [PartDesign::Pocket] Pocket017  label="emprunte001"
  AllowMultiFace = false
  BaseFeature = -> Pad022
  Direction = (1,1,1)
  Length = 4
  Length2 = 100
  Profile = -> Sketch038
  Type = 0
FEATURE [PartDesign::Body] Body010  label="visTHCM3x6_FAV002"
  Group = -> [Sketch036,Pad021,Sketch037,Pad022,DatumPlane015,Sketch038,Pocket017]
  Origin = -> Origin020
  Placement = pos=(-78.5,-61.8718,6.01041) rot=(1,0,0;3.92699rad)
  Tip = -> Pocket017
  expr: .Placement.Base.x = -(<<sp>>.largeurModuleBase - 6.5)
COMPONENT P15 — recipe-attached ("dissipPrt", modeled in this document).
Construction recipe (the document's own serialized feature program — sketch geometry with constraints, then the solid features built on it; lengths are millimeters unless a unit is written):

FEATURE [Sketcher::SketchObject] Sketch061
  FullyConstrained = true
  MapMode = 5
  Placement = pos=(0,0,0) rot=(1,0,0;1.5708rad)
  Support = -> [XZ_Plane028]
  sketch-geometry (16):
    g0: LineSegment StartX=-5.7 StartY=0 StartZ=0 EndX=5.7 EndY=0 EndZ=0
    g1: LineSegment StartX=5.7 StartY=0 StartZ=0 EndX=5.7 EndY=5.09 EndZ=0
    g2: LineSegment StartX=5.7 StartY=5.09 StartZ=0 EndX=4.56 EndY=5.09 EndZ=0
    g3: LineSegment StartX=4.56 StartY=5.09 StartZ=0 EndX=4.56 EndY=1.15 EndZ=0
    g4: LineSegment StartX=4.56 StartY=1.15 StartZ=0 EndX=2.29 EndY=1.15 EndZ=0
    g5: LineSegment StartX=2.29 StartY=1.15 StartZ=0 EndX=2.29 EndY=5.09 EndZ=0
    g6: LineSegment StartX=2.29 StartY=5.09 StartZ=0 EndX=1.15 EndY=5.09 EndZ=0
    g7: LineSegment StartX=1.15 StartY=5.09 StartZ=0 EndX=1.15 EndY=1.15 EndZ=0
    g8: LineSegment StartX=1.15 StartY=1.15 StartZ=0 EndX=-1.15 EndY=1.15 EndZ=0
    g9: LineSegment StartX=-1.15 StartY=1.15 StartZ=0 EndX=-1.15 EndY=5.09 EndZ=0
    g10: LineSegment StartX=-1.15 StartY=5.09 StartZ=0 EndX=-2.29 EndY=5.09 EndZ=0
    g11: LineSegment StartX=-2.29 StartY=5.09 StartZ=0 EndX=-2.29 EndY=1.15 EndZ=0
    g12: LineSegment StartX=-2.29 StartY=1.15 StartZ=0 EndX=-4.56 EndY=1.15 EndZ=0
    g13: LineSegment StartX=-4.56 StartY=1.15 StartZ=0 EndX=-4.56 EndY=5.09 EndZ=0
    g14: LineSegment StartX=-4.56 StartY=5.09 StartZ=0 EndX=-5.7 EndY=5.09 EndZ=0
    g15: LineSegment StartX=-5.7 StartY=5.09 StartZ=0 EndX=-5.7 EndY=0 EndZ=0
  constraints (46):
    c: PointOnObject(g0,g-1)
    c: Coincident(g0,g1)
    c: Vertical(g1)
    c: Coincident(g1,g2)
    c: Horizontal(g2)
    c: Coincident(g2,g3)
    c: Vertical(g3)
    c: Coincident(g3,g4)
    c: Coincident(g4,g5)
    c: Coincident(g5,g6)
    c: Coincident(g6,g7)
    c: Coincident(g7,g8)
    c: Coincident(g8,g9)
    c: Coincident(g9,g10)
    c: Horizontal(g10)
    c: Coincident(g10,g11)
    c: Coincident(g11,g12)
    c: Coincident(g12,g13)
    c: Coincident(g13,g14)
    c: Coincident(g14,g15)
    c: Coincident(g0,g15)
    c: Vertical(g15)
    c: Symmetric(g0,g0,g-2)
    c: Horizontal(g6)
    c: Horizontal(g4)
    c: Symmetric(g8,g7,g-2)
    c: DistanceX(g0,g0) = 11.4
    c: Vertical(g13)
    c: Horizontal(g14)
    c: Horizontal(g12)
    c: Horizontal(g13,g10)
    c: Horizontal(g9,g6)
    c: Vertical(g9)
    c: Vertical(g7)
    c: Vertical(g5)
    c: Horizontal(g5,g2)
    c: Horizontal(g11,g8)
    c: Horizontal(g7,g4)
    c: Vertical(g11)
    c: DistanceX(g2,g2) = 1.14
    c: Equal(g2,g6)
    c: Equal(g6,g10)
    c: Equal(g10,g14)
    c: DistanceX(g4,g4) = 2.27
    c: DistanceY(g0,g1) = 5.09
    c: DistanceY(g0,g12) = 1.15
FEATURE [PartDesign::Pad] Pad030
  Direction = (0,-1,-2e-16)
  Length = 7.2
  Length2 = 10
  Midplane = true
  Placement = pos=(0,0,0) rot=(1,0,0;1.5708rad)
  Profile = -> Sketch061
  ReferenceAxis = -> Sketch061 [N_Axis]
  Type = 0
  expr: Length = Spreadsheet003.Long
FEATURE [PartDesign::Fillet] Fillet001
  Base = -> Pad030 [Edge44,Edge41,Edge32,Edge29,Edge20,Edge17,Edge8,Edge5,Edge38,Edge26,Edge14,Edge35,Edge23,Edge11]
  BaseFeature = -> Pad030
  Placement = pos=(0,0,0) rot=(1,0,0;1.5708rad)
  Radius = 0.4
  SupportTransform = false
  UseAllEdges = false
FEATURE [PartDesign::Body] Body013  label="dissipBdy"
  Group = -> [Sketch061,Pad030,Fillet001]
  Origin = -> Origin032
  Tip = -> Fillet001
COMPONENT P16 — recipe-attached ("dissipPrt001", modeled in this document).
Construction recipe (the document's own serialized feature program — sketch geometry with constraints, then the solid features built on it; lengths are millimeters unless a unit is written):

FEATURE [Sketcher::SketchObject] Sketch062
  FullyConstrained = true
  MapMode = 5
  Placement = pos=(0,0,0) rot=(1,0,0;1.5708rad)
  Support = -> [XZ_Plane030]
  sketch-geometry (16):
    g0: LineSegment StartX=-5.7 StartY=0 StartZ=0 EndX=5.7 EndY=0 EndZ=0
    g1: LineSegment StartX=5.7 StartY=0 StartZ=0 EndX=5.7 EndY=5.09 EndZ=0
    g2: LineSegment StartX=5.7 StartY=5.09 StartZ=0 EndX=4.56 EndY=5.09 EndZ=0
    g3: LineSegment StartX=4.56 StartY=5.09 StartZ=0 EndX=4.56 EndY=1.15 EndZ=0
    g4: LineSegment StartX=4.56 StartY=1.15 StartZ=0 EndX=2.29 EndY=1.15 EndZ=0
    g5: LineSegment StartX=2.29 StartY=1.15 StartZ=0 EndX=2.29 EndY=5.09 EndZ=0
    g6: LineSegment StartX=2.29 StartY=5.09 StartZ=0 EndX=1.15 EndY=5.09 EndZ=0
    g7: LineSegment StartX=1.15 StartY=5.09 StartZ=0 EndX=1.15 EndY=1.15 EndZ=0
    g8: LineSegment StartX=1.15 StartY=1.15 StartZ=0 EndX=-1.15 EndY=1.15 EndZ=0
    g9: LineSegment StartX=-1.15 StartY=1.15 StartZ=0 EndX=-1.15 EndY=5.09 EndZ=0
    g10: LineSegment StartX=-1.15 StartY=5.09 StartZ=0 EndX=-2.29 EndY=5.09 EndZ=0
    g11: LineSegment StartX=-2.29 StartY=5.09 StartZ=0 EndX=-2.29 EndY=1.15 EndZ=0
    g12: LineSegment StartX=-2.29 StartY=1.15 StartZ=0 EndX=-4.56 EndY=1.15 EndZ=0
    g13: LineSegment StartX=-4.56 StartY=1.15 StartZ=0 EndX=-4.56 EndY=5.09 EndZ=0
    g14: LineSegment StartX=-4.56 StartY=5.09 StartZ=0 EndX=-5.7 EndY=5.09 EndZ=0
    g15: LineSegment StartX=-5.7 StartY=5.09 StartZ=0 EndX=-5.7 EndY=0 EndZ=0
  constraints (46):
    c: PointOnObject(g0,g-1)
    c: Coincident(g0,g1)
    c: Vertical(g1)
    c: Coincident(g1,g2)
    c: Horizontal(g2)
    c: Coincident(g2,g3)
    c: Vertical(g3)
    c: Coincident(g3,g4)
    c: Coincident(g4,g5)
    c: Coincident(g5,g6)
    c: Coincident(g6,g7)
    c: Coincident(g7,g8)
    c: Coincident(g8,g9)
    c: Coincident(g9,g10)
    c: Horizontal(g10)
    c: Coincident(g10,g11)
    c: Coincident(g11,g12)
    c: Coincident(g12,g13)
    c: Coincident(g13,g14)
    c: Coincident(g14,g15)
    c: Coincident(g0,g15)
    c: Vertical(g15)
    c: Symmetric(g0,g0,g-2)
    c: Horizontal(g6)
    c: Horizontal(g4)
    c: Symmetric(g8,g7,g-2)
    c: DistanceX(g0,g0) = 11.4
    c: Vertical(g13)
    c: Horizontal(g14)
    c: Horizontal(g12)
    c: Horizontal(g13,g10)
    c: Horizontal(g9,g6)
    c: Vertical(g9)
    c: Vertical(g7)
    c: Vertical(g5)
    c: Horizontal(g5,g2)
    c: Horizontal(g11,g8)
    c: Horizontal(g7,g4)
    c: Vertical(g11)
    c: DistanceX(g2,g2) = 1.14
    c: Equal(g2,g6)
    c: Equal(g6,g10)
    c: Equal(g10,g14)
    c: DistanceX(g4,g4) = 2.27
    c: DistanceY(g0,g1) = 5.09
    c: DistanceY(g0,g12) = 1.15
FEATURE [PartDesign::Pad] Pad031
  Direction = (0,-1,-2e-16)
  Length = 16
  Length2 = 10
  Midplane = true
  Placement = pos=(0,0,0) rot=(1,0,0;1.5708rad)
  Profile = -> Sketch062
  ReferenceAxis = -> Sketch062 [N_Axis]
  Type = 0
  expr: Length = Spreadsheet004.Long
FEATURE [PartDesign::Fillet] Fillet002
  Base = -> Pad031 [Edge44,Edge41,Edge32,Edge29,Edge20,Edge17,Edge8,Edge5,Edge38,Edge26,Edge14,Edge35,Edge23,Edge11]
  BaseFeature = -> Pad031
  Placement = pos=(0,0,0) rot=(1,0,0;1.5708rad)
  Radius = 0.4
  SupportTransform = false
  UseAllEdges = false
FEATURE [PartDesign::Body] Body014  label="dissipBdy001"
  Group = -> [Sketch062,Pad031,Fillet002]
  Origin = -> Origin034
  Tip = -> Fillet002
COMPONENT P17 — recipe-attached ("dissipPrt002", modeled in this document).
Construction recipe (the document's own serialized feature program — sketch geometry with constraints, then the solid features built on it; lengths are millimeters unless a unit is written):

FEATURE [Sketcher::SketchObject] Sketch063
  FullyConstrained = true
  MapMode = 5
  Placement = pos=(0,0,0) rot=(1,0,0;1.5708rad)
  Support = -> [XZ_Plane032]
  sketch-geometry (16):
    g0: LineSegment StartX=-5.7 StartY=0 StartZ=0 EndX=5.7 EndY=0 EndZ=0
    g1: LineSegment StartX=5.7 StartY=0 StartZ=0 EndX=5.7 EndY=5.09 EndZ=0
    g2: LineSegment StartX=5.7 StartY=5.09 StartZ=0 EndX=4.56 EndY=5.09 EndZ=0
    g3: LineSegment StartX=4.56 StartY=5.09 StartZ=0 EndX=4.56 EndY=1.15 EndZ=0
    g4: LineSegment StartX=4.56 StartY=1.15 StartZ=0 EndX=2.29 EndY=1.15 EndZ=0
    g5: LineSegment StartX=2.29 StartY=1.15 StartZ=0 EndX=2.29 EndY=5.09 EndZ=0
    g6: LineSegment StartX=2.29 StartY=5.09 StartZ=0 EndX=1.15 EndY=5.09 EndZ=0
    g7: LineSegment StartX=1.15 StartY=5.09 StartZ=0 EndX=1.15 EndY=1.15 EndZ=0
    g8: LineSegment StartX=1.15 StartY=1.15 StartZ=0 EndX=-1.15 EndY=1.15 EndZ=0
    g9: LineSegment StartX=-1.15 StartY=1.15 StartZ=0 EndX=-1.15 EndY=5.09 EndZ=0
    g10: LineSegment StartX=-1.15 StartY=5.09 StartZ=0 EndX=-2.29 EndY=5.09 EndZ=0
    g11: LineSegment StartX=-2.29 StartY=5.09 StartZ=0 EndX=-2.29 EndY=1.15 EndZ=0
    g12: LineSegment StartX=-2.29 StartY=1.15 StartZ=0 EndX=-4.56 EndY=1.15 EndZ=0
    g13: LineSegment StartX=-4.56 StartY=1.15 StartZ=0 EndX=-4.56 EndY=5.09 EndZ=0
    g14: LineSegment StartX=-4.56 StartY=5.09 StartZ=0 EndX=-5.7 EndY=5.09 EndZ=0
    g15: LineSegment StartX=-5.7 StartY=5.09 StartZ=0 EndX=-5.7 EndY=0 EndZ=0
  constraints (46):
    c: PointOnObject(g0,g-1)
    c: Coincident(g0,g1)
    c: Vertical(g1)
    c: Coincident(g1,g2)
    c: Horizontal(g2)
    c: Coincident(g2,g3)
    c: Vertical(g3)
    c: Coincident(g3,g4)
    c: Coincident(g4,g5)
    c: Coincident(g5,g6)
    c: Coincident(g6,g7)
    c: Coincident(g7,g8)
    c: Coincident(g8,g9)
    c: Coincident(g9,g10)
    c: Horizontal(g10)
    c: Coincident(g10,g11)
    c: Coincident(g11,g12)
    c: Coincident(g12,g13)
    c: Coincident(g13,g14)
    c: Coincident(g14,g15)
    c: Coincident(g0,g15)
    c: Vertical(g15)
    c: Symmetric(g0,g0,g-2)
    c: Horizontal(g6)
    c: Horizontal(g4)
    c: Symmetric(g8,g7,g-2)
    c: DistanceX(g0,g0) = 11.4
    c: Vertical(g13)
    c: Horizontal(g14)
    c: Horizontal(g12)
    c: Horizontal(g13,g10)
    c: Horizontal(g9,g6)
    c: Vertical(g9)
    c: Vertical(g7)
    c: Vertical(g5)
    c: Horizontal(g5,g2)
    c: Horizontal(g11,g8)
    c: Horizontal(g7,g4)
    c: Vertical(g11)
    c: DistanceX(g2,g2) = 1.14
    c: Equal(g2,g6)
    c: Equal(g6,g10)
    c: Equal(g10,g14)
    c: DistanceX(g4,g4) = 2.27
    c: DistanceY(g0,g1) = 5.09
    c: DistanceY(g0,g12) = 1.15
FEATURE [PartDesign::Pad] Pad032
  Direction = (0,-1,-2e-16)
  Length = 3.87
  Length2 = 10
  Midplane = true
  Placement = pos=(0,0,0) rot=(1,0,0;1.5708rad)
  Profile = -> Sketch063
  ReferenceAxis = -> Sketch063 [N_Axis]
  Type = 0
  expr: Length = Spreadsheet005.Long
FEATURE [PartDesign::Fillet] Fillet003
  Base = -> Pad032 [Edge44,Edge41,Edge32,Edge29,Edge20,Edge17,Edge8,Edge5,Edge38,Edge26,Edge14,Edge35,Edge23,Edge11]
  BaseFeature = -> Pad032
  Placement = pos=(0,0,0) rot=(1,0,0;1.5708rad)
  Radius = 0.4
  SupportTransform = false
  UseAllEdges = false
FEATURE [PartDesign::Body] Body015  label="dissipBdy002"
  Group = -> [Sketch063,Pad032,Fillet003]
  Origin = -> Origin036
  Tip = -> Fillet003
COMPONENT P18 — recipe-attached ("dissipPrt004", modeled in this document).
Construction recipe (the document's own serialized feature program — sketch geometry with constraints, then the solid features built on it; lengths are millimeters unless a unit is written):

FEATURE [Sketcher::SketchObject] Sketch065
  FullyConstrained = true
  MapMode = 5
  Placement = pos=(0,0,0) rot=(1,0,0;1.5708rad)
  Support = -> [XZ_Plane036]
  sketch-geometry (16):
    g0: LineSegment StartX=-5.7 StartY=0 StartZ=0 EndX=5.7 EndY=0 EndZ=0
    g1: LineSegment StartX=5.7 StartY=0 StartZ=0 EndX=5.7 EndY=5.09 EndZ=0
    g2: LineSegment StartX=5.7 StartY=5.09 StartZ=0 EndX=4.56 EndY=5.09 EndZ=0
    g3: LineSegment StartX=4.56 StartY=5.09 StartZ=0 EndX=4.56 EndY=1.15 EndZ=0
    g4: LineSegment StartX=4.56 StartY=1.15 StartZ=0 EndX=2.29 EndY=1.15 EndZ=0
    g5: LineSegment StartX=2.29 StartY=1.15 StartZ=0 EndX=2.29 EndY=5.09 EndZ=0
    g6: LineSegment StartX=2.29 StartY=5.09 StartZ=0 EndX=1.15 EndY=5.09 EndZ=0
    g7: LineSegment StartX=1.15 StartY=5.09 StartZ=0 EndX=1.15 EndY=1.15 EndZ=0
    g8: LineSegment StartX=1.15 StartY=1.15 StartZ=0 EndX=-1.15 EndY=1.15 EndZ=0
    g9: LineSegment StartX=-1.15 StartY=1.15 StartZ=0 EndX=-1.15 EndY=5.09 EndZ=0
    g10: LineSegment StartX=-1.15 StartY=5.09 StartZ=0 EndX=-2.29 EndY=5.09 EndZ=0
    g11: LineSegment StartX=-2.29 StartY=5.09 StartZ=0 EndX=-2.29 EndY=1.15 EndZ=0
    g12: LineSegment StartX=-2.29 StartY=1.15 StartZ=0 EndX=-4.56 EndY=1.15 EndZ=0
    g13: LineSegment StartX=-4.56 StartY=1.15 StartZ=0 EndX=-4.56 EndY=5.09 EndZ=0
    g14: LineSegment StartX=-4.56 StartY=5.09 StartZ=0 EndX=-5.7 EndY=5.09 EndZ=0
    g15: LineSegment StartX=-5.7 StartY=5.09 StartZ=0 EndX=-5.7 EndY=0 EndZ=0
  constraints (46):
    c: PointOnObject(g0,g-1)
    c: Coincident(g0,g1)
    c: Vertical(g1)
    c: Coincident(g1,g2)
    c: Horizontal(g2)
    c: Coincident(g2,g3)
    c: Vertical(g3)
    c: Coincident(g3,g4)
    c: Coincident(g4,g5)
    c: Coincident(g5,g6)
    c: Coincident(g6,g7)
    c: Coincident(g7,g8)
    c: Coincident(g8,g9)
    c: Coincident(g9,g10)
    c: Horizontal(g10)
    c: Coincident(g10,g11)
    c: Coincident(g11,g12)
    c: Coincident(g12,g13)
    c: Coincident(g13,g14)
    c: Coincident(g14,g15)
    c: Coincident(g0,g15)
    c: Vertical(g15)
    c: Symmetric(g0,g0,g-2)
    c: Horizontal(g6)
    c: Horizontal(g4)
    c: Symmetric(g8,g7,g-2)
    c: DistanceX(g0,g0) = 11.4
    c: Vertical(g13)
    c: Horizontal(g14)
    c: Horizontal(g12)
    c: Horizontal(g13,g10)
    c: Horizontal(g9,g6)
    c: Vertical(g9)
    c: Vertical(g7)
    c: Vertical(g5)
    c: Horizontal(g5,g2)
    c: Horizontal(g11,g8)
    c: Horizontal(g7,g4)
    c: Vertical(g11)
    c: DistanceX(g2,g2) = 1.14
    c: Equal(g2,g6)
    c: Equal(g6,g10)
    c: Equal(g10,g14)
    c: DistanceX(g4,g4) = 2.27
    c: DistanceY(g0,g1) = 5.09
    c: DistanceY(g0,g12) = 1.15
FEATURE [PartDesign::Pad] Pad034
  Direction = (0,-1,-2e-16)
  Length = 8
  Length2 = 10
  Midplane = true
  Placement = pos=(0,0,0) rot=(1,0,0;1.5708rad)
  Profile = -> Sketch065
  ReferenceAxis = -> Sketch065 [N_Axis]
  Type = 0
  expr: Length = Spreadsheet007.Long
FEATURE [PartDesign::Fillet] Fillet005
  Base = -> Pad034 [Edge44,Edge41,Edge32,Edge29,Edge20,Edge17,Edge8,Edge5,Edge38,Edge26,Edge14,Edge35,Edge23,Edge11]
  BaseFeature = -> Pad034
  Placement = pos=(0,0,0) rot=(1,0,0;1.5708rad)
  Radius = 0.4
  SupportTransform = false
  UseAllEdges = false
FEATURE [PartDesign::Body] Body017  label="dissipBdy004"
  Group = -> [Sketch065,Pad034,Fillet005]
  Origin = -> Origin040
  Tip = -> Fillet005
COMPONENT P19 — geometry summary ("dcdcWithDissip"; no construction recipe available for this part):
  bounding box: 54.0 x 50.3 x 14.8 mm
  tessellated surface: 482,406 triangles
  volume: 9310 mm^3 (23% of its bounding box)
PROVENANCE & LICENSES
A FreeCAD (.FCStd) document from a public repository crawl; recipes are the document's own serialized feature recipes (and, for linked parts, companion documents' recipes).
License: as declared in the source repository (recorded in the dataset sidecar).
